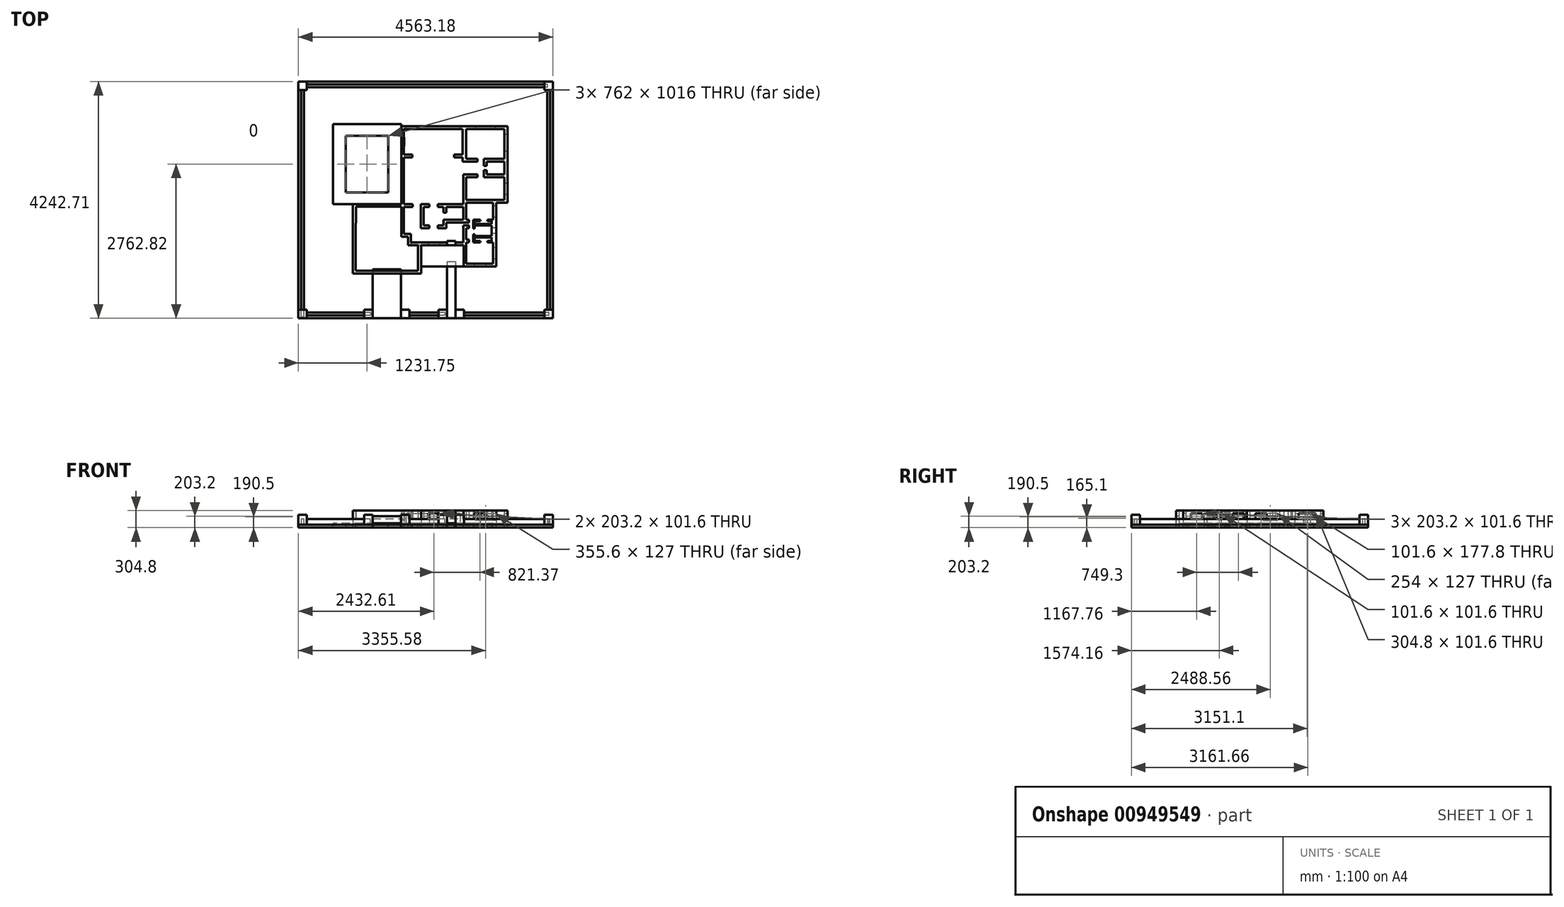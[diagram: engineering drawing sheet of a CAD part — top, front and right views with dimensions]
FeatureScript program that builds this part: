
annotation { "Feature Type Name" : "Feature", "Feature Type Description" : "" }
export const myFeature = defineFeature(function(context is Context, id is Id, definition is map)
    precondition{}
    {
        {
            var Q0;
            Q0=qCreatedBy(makeId("Top.planeOp"),FACE);
            var sketch = newSketch(context, id + "F0", { "sketchPlane" : qUnion([Q0])});
            skLineSegment(sketch, "E0", {"start": v(0, 0) * mm, "end": v(533.4, 0) * mm});
            skLineSegment(sketch, "E1", {"start": v(1396.8, 508) * mm, "end": v(1396.8, 127) * mm});
            skLineSegment(sketch, "E2", {"start": v(1396.8, 127) * mm, "end": v(1879.4, 127) * mm});
            skLineSegment(sketch, "E3", {"start": v(1828.6, 1270) * mm, "end": v(2082.6, 1270) * mm});
            skLineSegment(sketch, "E4", {"start": v(2082.6, 2540) * mm, "end": v(1396.8, 2540) * mm});
            skLineSegment(sketch, "E5", {"start": v(231.53, 1150.6) * mm, "end": v(-301.87, 1150.6) * mm});
            skLineSegment(sketch, "E6", {"start": v(-304.8, 1192.71) * mm, "end": v(177.8, 1192.71) * mm});
            skLineSegment(sketch, "E7", {"start": v(-47.87, -51.89) * mm, "end": v(587.13, -51.89) * mm});
            skLineSegment(sketch, "E8", {"start": v(587.13, -51.89) * mm, "end": v(587.13, 456.11) * mm});
            skLineSegment(sketch, "E9", {"start": v(587.13, 456.11) * mm, "end": v(1349.13, 456.11) * mm});
            skLineSegment(sketch, "E10", {"start": v(1349.13, 456.11) * mm, "end": v(1349.13, 75.11) * mm});
            skLineSegment(sketch, "E11", {"start": v(1349.13, 75.11) * mm, "end": v(1933.33, 75.11) * mm});
            skLineSegment(sketch, "E12", {"start": v(2136.53, 1218.11) * mm, "end": v(2136.53, 2589.71) * mm});
            skLineSegment(sketch, "E13", {"start": v(2136.53, 2589.71) * mm, "end": v(1349.13, 2589.71) * mm});
            skLineSegment(sketch, "E14", {"start": v(533.4, 456.11) * mm, "end": v(482.6, 456.11) * mm});
            skLineSegment(sketch, "E15", {"start": v(482.6, 456.11) * mm, "end": v(355.6, 456.11) * mm});
            skLineSegment(sketch, "E16", {"start": v(355.6, 456.11) * mm, "end": v(355.6, 608.51) * mm});
            skLineSegment(sketch, "E17", {"start": v(355.6, 608.51) * mm, "end": v(231.53, 608.51) * mm});
            skLineSegment(sketch, "E18", {"start": v(231.53, 608.51) * mm, "end": v(231.53, 1150.6) * mm});
            skLineSegment(sketch, "E19", {"start": v(279.4, 1143) * mm, "end": v(279.4, 660.4) * mm});
            skLineSegment(sketch, "E20", {"start": v(406.4, 508) * mm, "end": v(533.4, 508) * mm});
            skLineSegment(sketch, "E21", {"start": v(177.8, 1192.71) * mm, "end": v(231.53, 1192.71) * mm});
            skLineSegment(sketch, "E22", {"start": v(231.53, 1192.71) * mm, "end": v(231.53, 2081.71) * mm});
            skLineSegment(sketch, "E23", {"start": v(533.4, 456.11) * mm, "end": v(533.4, 0) * mm});
            skLineSegment(sketch, "E24", {"start": v(1828.6, 1219.2) * mm, "end": v(1396.8, 1219.2) * mm});
            skLineSegment(sketch, "E25", {"start": v(1933.33, 75.11) * mm, "end": v(1933.33, 1218.11) * mm});
            skLineSegment(sketch, "E26", {"start": v(1933.33, 1218.11) * mm, "end": v(2136.53, 1218.11) * mm});
            skLineSegment(sketch, "E27", {"start": v(1879.4, 127) * mm, "end": v(1879.4, 1219.2) * mm});
            skLineSegment(sketch, "E28", {"start": v(1879.4, 1219.2) * mm, "end": v(1828.6, 1219.2) * mm});
            skLineSegment(sketch, "E29", {"start": v(1396.8, 508) * mm, "end": v(1447.6, 508) * mm});
            skLineSegment(sketch, "E30", {"start": v(1523.8, 508) * mm, "end": v(1650.8, 508) * mm});
            skLineSegment(sketch, "E31", {"start": v(1879.4, 508) * mm, "end": v(1777.8, 508) * mm});
            skLineSegment(sketch, "E32", {"start": v(1523.8, 508) * mm, "end": v(1523.8, 596.9) * mm});
            skLineSegment(sketch, "E33", {"start": v(1879.4, 811.34) * mm, "end": v(1879.4, 749.31) * mm});
            skLineSegment(sketch, "E34", {"start": v(1523.8, 914.4) * mm, "end": v(1650.8, 914.4) * mm});
            skLineSegment(sketch, "E35", {"start": v(1879.4, 914.4) * mm, "end": v(1777.8, 914.4) * mm});
            skLineSegment(sketch, "E36", {"start": v(1523.8, 596.9) * mm, "end": v(1523.8, 650.75) * mm});
            skLineSegment(sketch, "E37", {"start": v(1523.8, 811.34) * mm, "end": v(1523.8, 757.49) * mm});
            skLineSegment(sketch, "E38", {"start": v(1396.8, 965.2) * mm, "end": v(1396.8, 1219.2) * mm});
            skLineSegment(sketch, "E39", {"start": v(1650.8, 914.4) * mm, "end": v(1650.8, 889) * mm});
            skLineSegment(sketch, "E40", {"start": v(1650.8, 889) * mm, "end": v(1549.2, 889) * mm});
            skLineSegment(sketch, "E41", {"start": v(1549.2, 889) * mm, "end": v(1549.2, 838.2) * mm});
            skLineSegment(sketch, "E42", {"start": v(1549.2, 838.2) * mm, "end": v(1854, 838.2) * mm});
            skLineSegment(sketch, "E43", {"start": v(1854, 838.2) * mm, "end": v(1854, 889) * mm});
            skLineSegment(sketch, "E44", {"start": v(1854, 889) * mm, "end": v(1777.8, 889) * mm});
            skLineSegment(sketch, "E45", {"start": v(1777.8, 889) * mm, "end": v(1777.8, 914.4) * mm});
            skLineSegment(sketch, "E46", {"start": v(1523.8, 757.49) * mm, "end": v(1549.2, 757.49) * mm});
            skLineSegment(sketch, "E47", {"start": v(1549.2, 757.49) * mm, "end": v(1549.2, 811.34) * mm});
            skLineSegment(sketch, "E48", {"start": v(1549.2, 811.34) * mm, "end": v(1854, 811.34) * mm});
            skLineSegment(sketch, "E49", {"start": v(1854, 811.34) * mm, "end": v(1854, 622.3) * mm});
            skLineSegment(sketch, "E50", {"start": v(1854, 622.3) * mm, "end": v(1549.2, 622.3) * mm});
            skLineSegment(sketch, "E51", {"start": v(1549.2, 622.3) * mm, "end": v(1549.2, 650.75) * mm});
            skLineSegment(sketch, "E52", {"start": v(1549.2, 650.75) * mm, "end": v(1523.8, 650.75) * mm});
            skLineSegment(sketch, "E53", {"start": v(1650.8, 508) * mm, "end": v(1650.8, 533.4) * mm});
            skLineSegment(sketch, "E54", {"start": v(1650.8, 533.4) * mm, "end": v(1549.2, 533.4) * mm});
            skLineSegment(sketch, "E55", {"start": v(1549.2, 533.4) * mm, "end": v(1549.2, 596.9) * mm});
            skLineSegment(sketch, "E56", {"start": v(1549.2, 596.9) * mm, "end": v(1854, 596.9) * mm});
            skLineSegment(sketch, "E57", {"start": v(1854, 596.9) * mm, "end": v(1854, 533.4) * mm});
            skLineSegment(sketch, "E58", {"start": v(1854, 533.4) * mm, "end": v(1777.8, 533.4) * mm});
            skLineSegment(sketch, "E59", {"start": v(1777.8, 533.4) * mm, "end": v(1777.8, 508) * mm});
            skLineSegment(sketch, "E60", {"start": v(1447.6, 508) * mm, "end": v(1447.6, 558.8) * mm});
            skLineSegment(sketch, "E61", {"start": v(1447.6, 558.8) * mm, "end": v(1396.8, 558.8) * mm});
            skLineSegment(sketch, "E62", {"start": v(1396.8, 558.8) * mm, "end": v(1396.8, 762) * mm});
            skLineSegment(sketch, "E63", {"start": v(1396.8, 965.2) * mm, "end": v(1396.8, 914.4) * mm});
            skLineSegment(sketch, "E64", {"start": v(1714.5, 1678.02) * mm, "end": v(2082.6, 1678.02) * mm});
            skLineSegment(sketch, "E65", {"start": v(1331.87, 2032) * mm, "end": v(1331.87, 1957.42) * mm});
            skLineSegment(sketch, "E66", {"start": v(1331.87, 1957.42) * mm, "end": v(1600.2, 1957.42) * mm});
            skLineSegment(sketch, "E67", {"start": v(1600.2, 1957.42) * mm, "end": v(1600.2, 2008.22) * mm});
            skLineSegment(sketch, "E68", {"start": v(1600.2, 2008.22) * mm, "end": v(1396.8, 2008.22) * mm});
            skLineSegment(sketch, "E69", {"start": v(1396.8, 2008.22) * mm, "end": v(1396.8, 2540) * mm});
            skLineSegment(sketch, "E70", {"start": v(1714.5, 1957.42) * mm, "end": v(1714.5, 2008.22) * mm});
            skLineSegment(sketch, "E71", {"start": v(1714.5, 2008.22) * mm, "end": v(2082.6, 2008.22) * mm});
            skLineSegment(sketch, "E72", {"start": v(2082.6, 2008.22) * mm, "end": v(2082.6, 2540) * mm});
            skLineSegment(sketch, "E73", {"start": v(1714.5, 1678.02) * mm, "end": v(1714.5, 1728.82) * mm});
            skLineSegment(sketch, "E74", {"start": v(2082.6, 1728.82) * mm, "end": v(2082.6, 1957.42) * mm});
            skLineSegment(sketch, "E75", {"start": v(2082.6, 1270) * mm, "end": v(2082.6, 1678.02) * mm});
            skLineSegment(sketch, "E76", {"start": v(1828.6, 1270) * mm, "end": v(1396.8, 1270) * mm});
            skLineSegment(sketch, "E77", {"start": v(1396.8, 1270) * mm, "end": v(1396.8, 1678.02) * mm});
            skLineSegment(sketch, "E78", {"start": v(1346, 1574.8) * mm, "end": v(1346, 1728.82) * mm});
            skLineSegment(sketch, "E79", {"start": v(1346, 1728.82) * mm, "end": v(1600.2, 1728.82) * mm});
            skLineSegment(sketch, "E80", {"start": v(1600.2, 1728.82) * mm, "end": v(1600.2, 1678.02) * mm});
            skLineSegment(sketch, "E81", {"start": v(1600.2, 1678.02) * mm, "end": v(1396.8, 1678.02) * mm});
            skLineSegment(sketch, "E82", {"start": v(1714.5, 1957.42) * mm, "end": v(1714.5, 1881.22) * mm});
            skLineSegment(sketch, "E83", {"start": v(1714.5, 1728.82) * mm, "end": v(1714.5, 1805.02) * mm});
            skLineSegment(sketch, "E84", {"start": v(1714.5, 1805.02) * mm, "end": v(1765.3, 1805.02) * mm});
            skLineSegment(sketch, "E85", {"start": v(1765.3, 1805.02) * mm, "end": v(1765.3, 1728.82) * mm});
            skLineSegment(sketch, "E86", {"start": v(1765.3, 1728.82) * mm, "end": v(2082.6, 1728.82) * mm});
            skLineSegment(sketch, "E87", {"start": v(1714.5, 1881.22) * mm, "end": v(1765.3, 1881.22) * mm});
            skLineSegment(sketch, "E88", {"start": v(1765.3, 1881.22) * mm, "end": v(1765.3, 1957.42) * mm});
            skLineSegment(sketch, "E89", {"start": v(1765.3, 1957.42) * mm, "end": v(2082.6, 1957.42) * mm});
            skLineSegment(sketch, "E90", {"start": v(-635, 508) * mm, "end": v(-635, 1192.71) * mm});
            skLineSegment(sketch, "E91", {"start": v(-635, 1192.71) * mm, "end": v(-304.8, 1192.71) * mm});
            skLineSegment(sketch, "E92", {"start": v(-301.87, 1150.6) * mm, "end": v(-581.27, 1150.6) * mm});
            skLineSegment(sketch, "E93", {"start": v(-584.2, 558.8) * mm, "end": v(-581.27, 1150.6) * mm});
            skLineSegment(sketch, "E94", {"start": v(-47.87, -51.89) * mm, "end": v(-635, -51.89) * mm});
            skLineSegment(sketch, "E95", {"start": v(-635, -51.89) * mm, "end": v(-635, 508) * mm});
            skLineSegment(sketch, "E96", {"start": v(0, 0) * mm, "end": v(-584.2, 0) * mm});
            skLineSegment(sketch, "E97", {"start": v(-584.2, 0) * mm, "end": v(-584.2, 558.8) * mm});
            skLineSegment(sketch, "E98", {"start": v(1331.87, 2032) * mm, "end": v(1179.47, 2032) * mm});
            skLineSegment(sketch, "E99", {"start": v(1179.47, 2032) * mm, "end": v(1179.47, 2081.71) * mm});
            skLineSegment(sketch, "E100", {"start": v(279.4, 2032) * mm, "end": v(431.8, 2032) * mm});
            skLineSegment(sketch, "E101", {"start": v(431.8, 2032) * mm, "end": v(431.8, 2081.71) * mm});
            skLineSegment(sketch, "E102", {"start": v(431.8, 2081.71) * mm, "end": v(279.4, 2081.71) * mm});
            skLineSegment(sketch, "E103", {"start": v(1179.47, 2081.71) * mm, "end": v(1331.87, 2081.71) * mm});
            skLineSegment(sketch, "E104", {"start": v(1331.87, 2081.71) * mm, "end": v(1331.87, 2540) * mm});
            skLineSegment(sketch, "E105", {"start": v(1331.87, 2540) * mm, "end": v(1179.47, 2540) * mm});
            skLineSegment(sketch, "E106", {"start": v(1179.47, 2589.71) * mm, "end": v(1349.13, 2589.71) * mm});
            skLineSegment(sketch, "E107", {"start": v(231.53, 2081.71) * mm, "end": v(231.53, 2589.71) * mm});
            skLineSegment(sketch, "E108", {"start": v(231.53, 2589.71) * mm, "end": v(431.8, 2589.71) * mm});
            skLineSegment(sketch, "E109", {"start": v(431.8, 2538.91) * mm, "end": v(279.4, 2538.91) * mm});
            skLineSegment(sketch, "E110", {"start": v(279.4, 2538.91) * mm, "end": v(279.4, 2081.71) * mm});
            skLineSegment(sketch, "E111", {"start": v(1346, 762) * mm, "end": v(1346, 508) * mm});
            skLineSegment(sketch, "E112", {"start": v(1346, 508) * mm, "end": v(533.4, 508) * mm});
            skLineSegment(sketch, "E113", {"start": v(1346, 863.6) * mm, "end": v(1396.8, 863.6) * mm});
            skLineSegment(sketch, "E114", {"start": v(1523.8, 811.34) * mm, "end": v(1523.8, 863.6) * mm});
            skLineSegment(sketch, "E115", {"start": v(1523.8, 863.6) * mm, "end": v(1523.8, 914.4) * mm});
            skLineSegment(sketch, "E116", {"start": v(1396.8, 914.4) * mm, "end": v(1447.6, 914.4) * mm});
            skLineSegment(sketch, "E117", {"start": v(1447.6, 914.4) * mm, "end": v(1447.6, 863.6) * mm});
            skLineSegment(sketch, "E118", {"start": v(1447.6, 863.6) * mm, "end": v(1396.8, 863.6) * mm});
            skLineSegment(sketch, "E119", {"start": v(406.4, 508) * mm, "end": v(406.4, 660.4) * mm});
            skLineSegment(sketch, "E120", {"start": v(406.4, 660.4) * mm, "end": v(279.4, 660.4) * mm});
            skLineSegment(sketch, "E121", {"start": v(1396.8, 812.8) * mm, "end": v(1447.6, 812.8) * mm});
            skLineSegment(sketch, "E122", {"start": v(1447.6, 812.8) * mm, "end": v(1447.6, 762) * mm});
            skLineSegment(sketch, "E123", {"start": v(1447.6, 762) * mm, "end": v(1396.8, 762) * mm});
            skLineSegment(sketch, "E124", {"start": v(431.8, 2538.91) * mm, "end": v(1179.47, 2540) * mm});
            skLineSegment(sketch, "E125", {"start": v(1179.47, 2589.71) * mm, "end": v(431.8, 2589.71) * mm});
            skLineSegment(sketch, "E126", {"start": v(1346, 812.8) * mm, "end": v(1396.8, 812.8) * mm});
            skLineSegment(sketch, "E127", {"start": v(1346, 508) * mm, "end": v(1041.2, 508) * mm});
            skLineSegment(sketch, "E128", {"start": v(887.59, 812.8) * mm, "end": v(887.59, 762) * mm});
            skLineSegment(sketch, "E129", {"start": v(887.59, 812.8) * mm, "end": v(938.39, 812.8) * mm});
            skLineSegment(sketch, "E130", {"start": v(1346, 1574.8) * mm, "end": v(1346, 1320.8) * mm});
            skLineSegment(sketch, "E131", {"start": v(887.59, 762) * mm, "end": v(1039.99, 762) * mm});
            skLineSegment(sketch, "E132", {"start": v(1039.99, 762) * mm, "end": v(1039.99, 812.8) * mm});
            skLineSegment(sketch, "E133", {"start": v(1346, 1320.8) * mm, "end": v(1346, 1270) * mm});
            skLineSegment(sketch, "E134", {"start": v(735.19, 762) * mm, "end": v(582.79, 762) * mm});
            skLineSegment(sketch, "E135", {"start": v(582.79, 762) * mm, "end": v(582.79, 812.8) * mm});
            skLineSegment(sketch, "E136", {"start": v(735.19, 812.8) * mm, "end": v(735.19, 762) * mm});
            skLineSegment(sketch, "E137", {"start": v(279.4, 1143) * mm, "end": v(437.73, 1143) * mm});
            skLineSegment(sketch, "E138", {"start": v(735.19, 1143) * mm, "end": v(735.19, 1193.8) * mm});
            skLineSegment(sketch, "E139", {"start": v(735.19, 1193.8) * mm, "end": v(582.79, 1193.8) * mm});
            skLineSegment(sketch, "E140", {"start": v(582.79, 1193.8) * mm, "end": v(582.79, 1143) * mm});
            skLineSegment(sketch, "E141", {"start": v(437.73, 1143) * mm, "end": v(437.73, 1193.8) * mm});
            skLineSegment(sketch, "E142", {"start": v(437.73, 1193.8) * mm, "end": v(279.4, 1193.8) * mm});
            skLineSegment(sketch, "E143", {"start": v(938.39, 812.8) * mm, "end": v(989.19, 812.8) * mm});
            skLineSegment(sketch, "E144", {"start": v(582.79, 812.8) * mm, "end": v(582.79, 1143) * mm});
            skLineSegment(sketch, "E145", {"start": v(633.59, 1143) * mm, "end": v(633.59, 812.8) * mm});
            skLineSegment(sketch, "E146", {"start": v(1039.99, 1193.8) * mm, "end": v(887.59, 1193.8) * mm});
            skLineSegment(sketch, "E147", {"start": v(887.59, 1193.8) * mm, "end": v(887.59, 1143) * mm});
            skLineSegment(sketch, "E148", {"start": v(887.59, 1143) * mm, "end": v(989.19, 1143) * mm});
            skLineSegment(sketch, "E149", {"start": v(633.59, 1143) * mm, "end": v(735.19, 1143) * mm});
            skLineSegment(sketch, "E150", {"start": v(633.59, 812.8) * mm, "end": v(735.19, 812.8) * mm});
            skLineSegment(sketch, "E151", {"start": v(279.4, 2032) * mm, "end": v(279.4, 1193.8) * mm});
            skLineSegment(sketch, "E152", {"start": v(1346, 1193.8) * mm, "end": v(1193.6, 1193.8) * mm});
            skPoint(sketch, "E152.startSnap0", {"position": v(963.79, 1193.8) * mm});
            skPoint(sketch, "E152.endSnap0", {"position": v(358.57, 1193.8) * mm});
            skLineSegment(sketch, "E153", {"start": v(1193.6, 1143) * mm, "end": v(1346, 1143) * mm});
            skLineSegment(sketch, "E154", {"start": v(1346, 1193.8) * mm, "end": v(1346, 1270) * mm});
            skLineSegment(sketch, "E155", {"start": v(1346, 762) * mm, "end": v(1346, 812.8) * mm});
            skLineSegment(sketch, "E156", {"start": v(1039.99, 1193.8) * mm, "end": v(1193.6, 1193.8) * mm});
            skLineSegment(sketch, "E157", {"start": v(1193.6, 1143) * mm, "end": v(1039.99, 1143) * mm});
            skLineSegment(sketch, "E158", {"start": v(1039.99, 863.6) * mm, "end": v(1039.99, 812.8) * mm});
            skLineSegment(sketch, "E159", {"start": v(1346, 939.8) * mm, "end": v(1346, 1117.6) * mm});
            skLineSegment(sketch, "E160", {"start": v(1346, 1117.6) * mm, "end": v(1346, 1143) * mm});
            skLineSegment(sketch, "E161", {"start": v(1346, 914.4) * mm, "end": v(1346, 939.8) * mm});
            skLineSegment(sketch, "E162", {"start": v(1346, 863.6) * mm, "end": v(1039.99, 863.6) * mm});
            skLineSegment(sketch, "E163", {"start": v(1346, 914.4) * mm, "end": v(1039.99, 914.4) * mm});
            skLineSegment(sketch, "E164", {"start": v(989.19, 914.4) * mm, "end": v(1039.99, 914.4) * mm});
            skLineSegment(sketch, "E165", {"start": v(989.19, 812.8) * mm, "end": v(989.19, 914.4) * mm});
            skLineSegment(sketch, "E166", {"start": v(989.19, 1143) * mm, "end": v(989.19, 1041.4) * mm});
            skLineSegment(sketch, "E167", {"start": v(989.19, 1041.4) * mm, "end": v(1039.99, 1041.4) * mm});
            skLineSegment(sketch, "E168", {"start": v(1039.99, 1041.4) * mm, "end": v(1039.99, 1143) * mm});
            skSolve(sketch);
        }
        {
            var Q0;
            Q0=makeQuery(id+"F0.imprint","IMPRINT",FACE,{"disambiguationData":[TD([[makeQuery(id+"F0.imprint","IMPRINT",EDGE,{"derivedFrom":sQuery(id+"F0.wireOp",EDGE,"E0")}),-1.0]])]});
            var Q1;
            Q1=makeQuery(id+"F0.imprint","IMPRINT",FACE,{"disambiguationData":[TD([[makeQuery(id+"F0.imprint","IMPRINT",EDGE,{"derivedFrom":sQuery(id+"F0.wireOp",EDGE,"E30")}),1.0]])]});
            extrude(context, id + "F1", {"entities" : qUnion([Q0, Q1]), "depth" : 254 * mm, "offsetDistance" : 25.4 * mm});
        }
        {
            var Q0;
            Q0=qSketchRegion(id+"F0",true);
            var Q1;
            Q1=makeQuery(id+"F0.imprint","IMPRINT",FACE,{"disambiguationData":[TD([[makeQuery(id+"F0.imprint","IMPRINT",EDGE,{"derivedFrom":sQuery(id+"F0.wireOp",EDGE,"E134")}),-1.0]])]});
            var Q2;
            Q2=makeQuery(id+"F0.imprint","IMPRINT",FACE,{"disambiguationData":[TD([[makeQuery(id+"F0.imprint","IMPRINT",EDGE,{"derivedFrom":sQuery(id+"F0.wireOp",EDGE,"E128")}),1.0]])]});
            extrude(context, id + "F2", {"entities" : qUnion([Q0, Q1, Q2]), "operationType" : NewBodyOperationType.ADD, "depth" : 254 * mm, "offsetDistance" : 25.4 * mm});
        }
        {
            var Q0;
            Q0=makeQuery(id+"F1.opExtrude","CAP_FACE",FACE,{"disambiguationData":[OSD([sQuery(id+"F0.wireOp",EDGE,"E0"),sQuery(id+"F0.wireOp",EDGE,"E1"),sQuery(id+"F0.wireOp",EDGE,"E2"),sQuery(id+"F0.wireOp",EDGE,"E3"),sQuery(id+"F0.wireOp",EDGE,"E4"),sQuery(id+"F0.wireOp",EDGE,"E5"),sQuery(id+"F0.wireOp",EDGE,"E6"),sQuery(id+"F0.wireOp",EDGE,"E7"),sQuery(id+"F0.wireOp",EDGE,"E8"),sQuery(id+"F0.wireOp",EDGE,"E9"),sQuery(id+"F0.wireOp",EDGE,"E10"),sQuery(id+"F0.wireOp",EDGE,"E11"),sQuery(id+"F0.wireOp",EDGE,"E12"),sQuery(id+"F0.wireOp",EDGE,"E13"),sQuery(id+"F0.wireOp",EDGE,"E14"),sQuery(id+"F0.wireOp",EDGE,"E15"),sQuery(id+"F0.wireOp",EDGE,"E16"),sQuery(id+"F0.wireOp",EDGE,"E17"),sQuery(id+"F0.wireOp",EDGE,"E18"),sQuery(id+"F0.wireOp",EDGE,"E19"),sQuery(id+"F0.wireOp",EDGE,"E20"),sQuery(id+"F0.wireOp",EDGE,"E21"),sQuery(id+"F0.wireOp",EDGE,"E22"),sQuery(id+"F0.wireOp",EDGE,"E23"),sQuery(id+"F0.wireOp",EDGE,"E24"),sQuery(id+"F0.wireOp",EDGE,"E25"),sQuery(id+"F0.wireOp",EDGE,"E26"),sQuery(id+"F0.wireOp",EDGE,"E27"),sQuery(id+"F0.wireOp",EDGE,"E28"),sQuery(id+"F0.wireOp",EDGE,"E29"),sQuery(id+"F0.wireOp",EDGE,"E30"),sQuery(id+"F0.wireOp",EDGE,"E31"),sQuery(id+"F0.wireOp",EDGE,"E32"),sQuery(id+"F0.wireOp",EDGE,"E34"),sQuery(id+"F0.wireOp",EDGE,"E35"),sQuery(id+"F0.wireOp",EDGE,"E36"),sQuery(id+"F0.wireOp",EDGE,"E37"),sQuery(id+"F0.wireOp",EDGE,"E38"),sQuery(id+"F0.wireOp",EDGE,"E39"),sQuery(id+"F0.wireOp",EDGE,"E40"),sQuery(id+"F0.wireOp",EDGE,"E41"),sQuery(id+"F0.wireOp",EDGE,"E42"),sQuery(id+"F0.wireOp",EDGE,"E43"),sQuery(id+"F0.wireOp",EDGE,"E44"),sQuery(id+"F0.wireOp",EDGE,"E45"),sQuery(id+"F0.wireOp",EDGE,"E46"),sQuery(id+"F0.wireOp",EDGE,"E47"),sQuery(id+"F0.wireOp",EDGE,"E48"),sQuery(id+"F0.wireOp",EDGE,"E49"),sQuery(id+"F0.wireOp",EDGE,"E50"),sQuery(id+"F0.wireOp",EDGE,"E51"),sQuery(id+"F0.wireOp",EDGE,"E52"),sQuery(id+"F0.wireOp",EDGE,"E53"),sQuery(id+"F0.wireOp",EDGE,"E54"),sQuery(id+"F0.wireOp",EDGE,"E55"),sQuery(id+"F0.wireOp",EDGE,"E56"),sQuery(id+"F0.wireOp",EDGE,"E57"),sQuery(id+"F0.wireOp",EDGE,"E58"),sQuery(id+"F0.wireOp",EDGE,"E59"),sQuery(id+"F0.wireOp",EDGE,"E60"),sQuery(id+"F0.wireOp",EDGE,"E61"),sQuery(id+"F0.wireOp",EDGE,"E62"),sQuery(id+"F0.wireOp",EDGE,"E63"),sQuery(id+"F0.wireOp",EDGE,"E64"),sQuery(id+"F0.wireOp",EDGE,"E65"),sQuery(id+"F0.wireOp",EDGE,"E66"),sQuery(id+"F0.wireOp",EDGE,"E67"),sQuery(id+"F0.wireOp",EDGE,"E68"),sQuery(id+"F0.wireOp",EDGE,"E69"),sQuery(id+"F0.wireOp",EDGE,"E70"),sQuery(id+"F0.wireOp",EDGE,"E71"),sQuery(id+"F0.wireOp",EDGE,"E72"),sQuery(id+"F0.wireOp",EDGE,"E73"),sQuery(id+"F0.wireOp",EDGE,"E74"),sQuery(id+"F0.wireOp",EDGE,"E75"),sQuery(id+"F0.wireOp",EDGE,"E76"),sQuery(id+"F0.wireOp",EDGE,"E77"),sQuery(id+"F0.wireOp",EDGE,"E78"),sQuery(id+"F0.wireOp",EDGE,"E79"),sQuery(id+"F0.wireOp",EDGE,"E80"),sQuery(id+"F0.wireOp",EDGE,"E81"),sQuery(id+"F0.wireOp",EDGE,"E82"),sQuery(id+"F0.wireOp",EDGE,"E83"),sQuery(id+"F0.wireOp",EDGE,"E84"),sQuery(id+"F0.wireOp",EDGE,"E85"),sQuery(id+"F0.wireOp",EDGE,"E86"),sQuery(id+"F0.wireOp",EDGE,"E87"),sQuery(id+"F0.wireOp",EDGE,"E88"),sQuery(id+"F0.wireOp",EDGE,"E89"),sQuery(id+"F0.wireOp",EDGE,"E90"),sQuery(id+"F0.wireOp",EDGE,"E91"),sQuery(id+"F0.wireOp",EDGE,"E92"),sQuery(id+"F0.wireOp",EDGE,"E93"),sQuery(id+"F0.wireOp",EDGE,"E94"),sQuery(id+"F0.wireOp",EDGE,"E95"),sQuery(id+"F0.wireOp",EDGE,"E96"),sQuery(id+"F0.wireOp",EDGE,"E97"),sQuery(id+"F0.wireOp",EDGE,"E98"),sQuery(id+"F0.wireOp",EDGE,"E99"),sQuery(id+"F0.wireOp",EDGE,"E100"),sQuery(id+"F0.wireOp",EDGE,"E101"),sQuery(id+"F0.wireOp",EDGE,"E102"),sQuery(id+"F0.wireOp",EDGE,"E103"),sQuery(id+"F0.wireOp",EDGE,"E104"),sQuery(id+"F0.wireOp",EDGE,"E105"),sQuery(id+"F0.wireOp",EDGE,"E106"),sQuery(id+"F0.wireOp",EDGE,"E107"),sQuery(id+"F0.wireOp",EDGE,"E108"),sQuery(id+"F0.wireOp",EDGE,"E109"),sQuery(id+"F0.wireOp",EDGE,"E110"),sQuery(id+"F0.wireOp",EDGE,"E111"),sQuery(id+"F0.wireOp",EDGE,"E112"),sQuery(id+"F0.wireOp",EDGE,"E113"),sQuery(id+"F0.wireOp",EDGE,"E114"),sQuery(id+"F0.wireOp",EDGE,"E115"),sQuery(id+"F0.wireOp",EDGE,"E116"),sQuery(id+"F0.wireOp",EDGE,"E117"),sQuery(id+"F0.wireOp",EDGE,"E118"),sQuery(id+"F0.wireOp",EDGE,"E119"),sQuery(id+"F0.wireOp",EDGE,"E120"),sQuery(id+"F0.wireOp",EDGE,"E121"),sQuery(id+"F0.wireOp",EDGE,"E122"),sQuery(id+"F0.wireOp",EDGE,"E123"),sQuery(id+"F0.wireOp",EDGE,"E124"),sQuery(id+"F0.wireOp",EDGE,"E125"),sQuery(id+"F0.wireOp",EDGE,"E126"),sQuery(id+"F0.wireOp",EDGE,"E127"),sQuery(id+"F0.wireOp",EDGE,"E130"),sQuery(id+"F0.wireOp",EDGE,"wEKJqsZE-Lnf2-Pc3B-vstB-3JEagEBnImep"),sQuery(id+"F0.wireOp",EDGE,"E133"),sQuery(id+"F0.wireOp",EDGE,"E137"),sQuery(id+"F0.wireOp",EDGE,"E141"),sQuery(id+"F0.wireOp",EDGE,"E142"),sQuery(id+"F0.wireOp",EDGE,"E151"),sQuery(id+"F0.wireOp",EDGE,"E152"),sQuery(id+"F0.wireOp",EDGE,"XqZMZlJO-xrwS-6yc9-YKlE-u4GM9skw6DG2"),sQuery(id+"F0.wireOp",EDGE,"E153"),sQuery(id+"F0.wireOp",EDGE,"E154"),sQuery(id+"F0.wireOp",EDGE,"MRLSVep9-wh13-aC8x-J69K-2GoYUCsBfXyJ"),sQuery(id+"F0.wireOp",EDGE,"E155")])],"isStart":true});
            var sketch = newSketch(context, id + "F3", { "sketchPlane" : qUnion([Q0])});
            skSolve(sketch);
        }
        {
            var Q0;
            Q0=makeQuery(id+"F3.imprint","IMPRINT",FACE,{"disambiguationData":[TD([[makeQuery(id+"F3.imprint","IMPRINT",EDGE,{"derivedFrom":makeQuery(id+"F1.opExtrude","CAP_EDGE",EDGE,{"disambiguationData":[OSD([sQuery(id+"F0.wireOp",EDGE,"E16")])],"isStart":true})}),-1.0]])]});
            var Q1;
            Q1=makeQuery(id+"F3.imprint","IMPRINT",FACE,{"disambiguationData":[TD([[makeQuery(id+"F3.imprint","IMPRINT",EDGE,{"derivedFrom":makeQuery(id+"F1.opExtrude","CAP_EDGE",EDGE,{"disambiguationData":[OSD([sQuery(id+"F0.wireOp",EDGE,"E1")])],"isStart":true})}),-1.0]])]});
            extrude(context, id + "F4", {"entities" : qUnion([Q0, Q1]), "oppositeDirection" : true, "depth" : 25.4 * mm, "offsetDistance" : 25.4 * mm});
        }
        {
            var Q0;
            Q0=makeQuery(id+"F1.opExtrude","SWEPT_FACE",FACE,{"disambiguationData":[OSD([sQuery(id+"F0.wireOp",EDGE,"E18")])]});
            var sketch = newSketch(context, id + "F5", { "sketchPlane" : qUnion([Q0])});
            skLineSegment(sketch, "E169", {"start": v(-608.51, 254) * mm, "end": v(-879.56, 254) * mm});
            skLineSegment(sketch, "E170", {"start": v(-879.56, 254) * mm, "end": v(-981.16, 254) * mm});
            skLineSegment(sketch, "E171", {"start": v(-981.16, 254) * mm, "end": v(-777.96, 254) * mm});
            skLineSegment(sketch, "E172", {"start": v(-777.96, 254) * mm, "end": v(-777.96, 25.4) * mm});
            skLineSegment(sketch, "E173", {"start": v(-777.96, 25.4) * mm, "end": v(-981.16, 25.4) * mm});
            skLineSegment(sketch, "E174", {"start": v(-981.16, 25.4) * mm, "end": v(-981.16, 254) * mm});
            skLineSegment(sketch, "E175", {"start": v(-981.16, 254) * mm, "end": v(-981.16, 203.2) * mm});
            skLineSegment(sketch, "E176", {"start": v(-981.16, 203.2) * mm, "end": v(-777.96, 203.2) * mm});
            skLineSegment(sketch, "E177", {"start": v(-777.96, 203.2) * mm, "end": v(-777.96, 254) * mm});
            skSolve(sketch);
        }
        {
            var Q0;
            Q0=qSketchRegion(id+"F5",true);
            extrude(context, id + "F6", {"entities" : qUnion([Q0]), "operationType" : NewBodyOperationType.REMOVE, "oppositeDirection" : true, "depth" : 50.8 * mm, "offsetDistance" : 25.4 * mm});
        }
        {
            var Q0;
            Q0=makeQuery(id+"F1.opExtrude","SWEPT_FACE",FACE,{"disambiguationData":[OSD([sQuery(id+"F0.wireOp",EDGE,"E9")])]});
            var sketch = newSketch(context, id + "F7", { "sketchPlane" : qUnion([Q0])});
            skLineSegment(sketch, "E178", {"start": v(1052.6, 0) * mm, "end": v(1052.6, 254) * mm});
            skLineSegment(sketch, "E179", {"start": v(1052.6, 254) * mm, "end": v(1205, 254) * mm});
            skLineSegment(sketch, "E180", {"start": v(1205, 254) * mm, "end": v(1205, 0) * mm});
            skLineSegment(sketch, "E181", {"start": v(1205, 0) * mm, "end": v(1052.6, 0) * mm});
            skSolve(sketch);
        }
        {
            var Q0;
            Q0=qSketchRegion(id+"F7",true);
            extrude(context, id + "F8", {"entities" : qUnion([Q0]), "operationType" : NewBodyOperationType.REMOVE, "oppositeDirection" : true, "depth" : 76.2 * mm, "offsetDistance" : 25.4 * mm});
        }
        {
            var Q0;
            Q0=makeQuery(id+"F4.opExtrude","SWEPT_FACE",FACE,{"disambiguationData":[OSD([sQuery(id+"F0.wireOp",EDGE,"E20"),sQuery(id+"F0.wireOp",EDGE,"E112"),sQuery(id+"F0.wireOp",EDGE,"E127")])]});
            var sketch = newSketch(context, id + "F9", { "sketchPlane" : qUnion([Q0])});
            skSolve(sketch);
        }
        {
            var Q0;
            Q0=qSketchRegion(id+"F9",true);
            var Q1;
            {var subQ0=sQuery(id+"F0.wireOp",EDGE,"E127");var subQ1=sQuery(id+"F0.wireOp",EDGE,"E112");var subQ2=sQuery(id+"F0.wireOp",EDGE,"E20");Q1=makeQuery(id+"F9.imprint","IMPRINT",FACE,{"disambiguationData":[TD([[makeQuery(id+"F9.imprint","IMPRINT",EDGE,{"derivedFrom":makeQuery(id+"F4.opExtrude","CAP_EDGE",EDGE,{"disambiguationData":[OSD([subQ2,subQ1,subQ0])],"isStart":true})}),-1.0]])]});}
            extrude(context, id + "F10", {"entities" : qUnion([Q0, Q1]), "depth" : 53.34 * mm, "offsetDistance" : 25.4 * mm});
        }
        {
            var Q0;
            {var subQ130=sQuery(id+"F0.wireOp",EDGE,"E9");var subQ131=sQuery(id+"F0.wireOp",EDGE,"E8");Q0=makeQuery(id+"F8.boolean.opBoolean","SPLIT",FACE,{"disambiguationData":[TD([makeQuery(id+"F1.opExtrude","SWEPT_FACE",FACE,{"disambiguationData":[OSD([subQ131])]})])],"derivedFrom":makeQuery(id+"F1.opExtrude","SWEPT_FACE",FACE,{"disambiguationData":[OSD([subQ130])]})});}
            var sketch = newSketch(context, id + "F11", { "sketchPlane" : qUnion([Q0])});
            skLineSegment(sketch, "E182", {"start": v(819.86, 203.2) * mm, "end": v(718.26, 203.2) * mm});
            skLineSegment(sketch, "E183", {"start": v(718.26, 203.2) * mm, "end": v(718.26, 101.6) * mm});
            skLineSegment(sketch, "E184", {"start": v(718.26, 101.6) * mm, "end": v(921.46, 101.6) * mm});
            skLineSegment(sketch, "E185", {"start": v(921.46, 101.6) * mm, "end": v(921.46, 203.2) * mm});
            skLineSegment(sketch, "E186", {"start": v(921.46, 203.2) * mm, "end": v(819.86, 203.2) * mm});
            skSolve(sketch);
        }
        {
            var Q0;
            Q0=qSketchRegion(id+"F11",true);
            extrude(context, id + "F12", {"entities" : qUnion([Q0]), "operationType" : NewBodyOperationType.REMOVE, "oppositeDirection" : true, "depth" : 63.5 * mm, "offsetDistance" : 25.4 * mm});
        }
        {
            var Q0;
            Q0=makeQuery(id+"F1.opExtrude","SWEPT_FACE",FACE,{"disambiguationData":[OSD([sQuery(id+"F0.wireOp",EDGE,"E11")])]});
            var sketch = newSketch(context, id + "F13", { "sketchPlane" : qUnion([Q0])});
            skLineSegment(sketch, "E187", {"start": v(1641.23, 203.2) * mm, "end": v(1539.63, 203.2) * mm});
            skLineSegment(sketch, "E188", {"start": v(1539.63, 203.2) * mm, "end": v(1539.63, 101.6) * mm});
            skLineSegment(sketch, "E189", {"start": v(1539.63, 101.6) * mm, "end": v(1742.83, 101.6) * mm});
            skLineSegment(sketch, "E190", {"start": v(1742.83, 101.6) * mm, "end": v(1742.83, 203.2) * mm});
            skLineSegment(sketch, "E191", {"start": v(1742.83, 203.2) * mm, "end": v(1641.23, 203.2) * mm});
            skSolve(sketch);
        }
        {
            var Q0;
            Q0=qSketchRegion(id+"F13",true);
            extrude(context, id + "F14", {"entities" : qUnion([Q0]), "operationType" : NewBodyOperationType.REMOVE, "oppositeDirection" : true, "depth" : 76.2 * mm, "offsetDistance" : 25.4 * mm});
        }
        {
            var Q0;
            Q0=makeQuery(id+"F1.opExtrude","SWEPT_FACE",FACE,{"disambiguationData":[OSD([sQuery(id+"F0.wireOp",EDGE,"E25")])]});
            var sketch = newSketch(context, id + "F15", { "sketchPlane" : qUnion([Q0])});
            skLineSegment(sketch, "E192", {"start": v(75.11, 254) * mm, "end": v(557.71, 254) * mm});
            skLineSegment(sketch, "E193", {"start": v(557.71, 254) * mm, "end": v(316.41, 254) * mm});
            skLineSegment(sketch, "E194", {"start": v(316.41, 203.2) * mm, "end": v(214.81, 203.2) * mm});
            skLineSegment(sketch, "E195", {"start": v(214.81, 203.2) * mm, "end": v(214.81, 101.6) * mm});
            skLineSegment(sketch, "E196", {"start": v(214.81, 101.6) * mm, "end": v(418.01, 101.6) * mm});
            skLineSegment(sketch, "E197", {"start": v(418.01, 101.6) * mm, "end": v(418.01, 203.2) * mm});
            skLineSegment(sketch, "E198", {"start": v(418.01, 203.2) * mm, "end": v(316.41, 203.2) * mm});
            skLineSegment(sketch, "E199", {"start": v(1218.11, 254) * mm, "end": v(913.31, 254) * mm});
            skLineSegment(sketch, "E200", {"start": v(1065.71, 203.2) * mm, "end": v(964.11, 203.2) * mm});
            skLineSegment(sketch, "E201", {"start": v(964.11, 203.2) * mm, "end": v(964.11, 101.6) * mm});
            skLineSegment(sketch, "E202", {"start": v(964.11, 101.6) * mm, "end": v(1167.31, 101.6) * mm});
            skLineSegment(sketch, "E203", {"start": v(1167.31, 101.6) * mm, "end": v(1167.31, 203.2) * mm});
            skLineSegment(sketch, "E204", {"start": v(1167.31, 203.2) * mm, "end": v(1065.71, 203.2) * mm});
            skLineSegment(sketch, "E205", {"start": v(913.31, 254) * mm, "end": v(862.51, 254) * mm});
            skLineSegment(sketch, "E206", {"start": v(862.51, 254) * mm, "end": v(557.71, 254) * mm});
            skLineSegment(sketch, "E207", {"start": v(710.11, 254) * mm, "end": v(710.11, 203.2) * mm});
            skLineSegment(sketch, "E208", {"start": v(710.11, 203.2) * mm, "end": v(672.01, 203.2) * mm});
            skLineSegment(sketch, "E209", {"start": v(672.01, 203.2) * mm, "end": v(672.01, 101.6) * mm});
            skLineSegment(sketch, "E210", {"start": v(672.01, 101.6) * mm, "end": v(773.61, 101.6) * mm});
            skLineSegment(sketch, "E211", {"start": v(773.61, 101.6) * mm, "end": v(773.61, 203.2) * mm});
            skLineSegment(sketch, "E212", {"start": v(773.61, 203.2) * mm, "end": v(710.11, 203.2) * mm});
            skSolve(sketch);
        }
        {
            var Q0;
            Q0=qSketchRegion(id+"F15",true);
            extrude(context, id + "F16", {"entities" : qUnion([Q0]), "operationType" : NewBodyOperationType.REMOVE, "oppositeDirection" : true, "depth" : 101.6 * mm, "offsetDistance" : 25.4 * mm});
        }
        {
            var Q0;
            Q0=makeQuery(id+"F1.opExtrude","CAP_FACE",FACE,{"disambiguationData":[OSD([sQuery(id+"F0.wireOp",EDGE,"E0"),sQuery(id+"F0.wireOp",EDGE,"E1"),sQuery(id+"F0.wireOp",EDGE,"E2"),sQuery(id+"F0.wireOp",EDGE,"E3"),sQuery(id+"F0.wireOp",EDGE,"E4"),sQuery(id+"F0.wireOp",EDGE,"E5"),sQuery(id+"F0.wireOp",EDGE,"E6"),sQuery(id+"F0.wireOp",EDGE,"E7"),sQuery(id+"F0.wireOp",EDGE,"E8"),sQuery(id+"F0.wireOp",EDGE,"E9"),sQuery(id+"F0.wireOp",EDGE,"E10"),sQuery(id+"F0.wireOp",EDGE,"E11"),sQuery(id+"F0.wireOp",EDGE,"E12"),sQuery(id+"F0.wireOp",EDGE,"E13"),sQuery(id+"F0.wireOp",EDGE,"E14"),sQuery(id+"F0.wireOp",EDGE,"E15"),sQuery(id+"F0.wireOp",EDGE,"E16"),sQuery(id+"F0.wireOp",EDGE,"E17"),sQuery(id+"F0.wireOp",EDGE,"E18"),sQuery(id+"F0.wireOp",EDGE,"E19"),sQuery(id+"F0.wireOp",EDGE,"E20"),sQuery(id+"F0.wireOp",EDGE,"E21"),sQuery(id+"F0.wireOp",EDGE,"E22"),sQuery(id+"F0.wireOp",EDGE,"E23"),sQuery(id+"F0.wireOp",EDGE,"E24"),sQuery(id+"F0.wireOp",EDGE,"E25"),sQuery(id+"F0.wireOp",EDGE,"E26"),sQuery(id+"F0.wireOp",EDGE,"E27"),sQuery(id+"F0.wireOp",EDGE,"E28"),sQuery(id+"F0.wireOp",EDGE,"E29"),sQuery(id+"F0.wireOp",EDGE,"E30"),sQuery(id+"F0.wireOp",EDGE,"E31"),sQuery(id+"F0.wireOp",EDGE,"E32"),sQuery(id+"F0.wireOp",EDGE,"E34"),sQuery(id+"F0.wireOp",EDGE,"E35"),sQuery(id+"F0.wireOp",EDGE,"E36"),sQuery(id+"F0.wireOp",EDGE,"E37"),sQuery(id+"F0.wireOp",EDGE,"E38"),sQuery(id+"F0.wireOp",EDGE,"E39"),sQuery(id+"F0.wireOp",EDGE,"E40"),sQuery(id+"F0.wireOp",EDGE,"E41"),sQuery(id+"F0.wireOp",EDGE,"E42"),sQuery(id+"F0.wireOp",EDGE,"E43"),sQuery(id+"F0.wireOp",EDGE,"E44"),sQuery(id+"F0.wireOp",EDGE,"E45"),sQuery(id+"F0.wireOp",EDGE,"E46"),sQuery(id+"F0.wireOp",EDGE,"E47"),sQuery(id+"F0.wireOp",EDGE,"E48"),sQuery(id+"F0.wireOp",EDGE,"E49"),sQuery(id+"F0.wireOp",EDGE,"E50"),sQuery(id+"F0.wireOp",EDGE,"E51"),sQuery(id+"F0.wireOp",EDGE,"E52"),sQuery(id+"F0.wireOp",EDGE,"E53"),sQuery(id+"F0.wireOp",EDGE,"E54"),sQuery(id+"F0.wireOp",EDGE,"E55"),sQuery(id+"F0.wireOp",EDGE,"E56"),sQuery(id+"F0.wireOp",EDGE,"E57"),sQuery(id+"F0.wireOp",EDGE,"E58"),sQuery(id+"F0.wireOp",EDGE,"E59"),sQuery(id+"F0.wireOp",EDGE,"E60"),sQuery(id+"F0.wireOp",EDGE,"E61"),sQuery(id+"F0.wireOp",EDGE,"E62"),sQuery(id+"F0.wireOp",EDGE,"E63"),sQuery(id+"F0.wireOp",EDGE,"E64"),sQuery(id+"F0.wireOp",EDGE,"E65"),sQuery(id+"F0.wireOp",EDGE,"E66"),sQuery(id+"F0.wireOp",EDGE,"E67"),sQuery(id+"F0.wireOp",EDGE,"E68"),sQuery(id+"F0.wireOp",EDGE,"E69"),sQuery(id+"F0.wireOp",EDGE,"E70"),sQuery(id+"F0.wireOp",EDGE,"E71"),sQuery(id+"F0.wireOp",EDGE,"E72"),sQuery(id+"F0.wireOp",EDGE,"E73"),sQuery(id+"F0.wireOp",EDGE,"E74"),sQuery(id+"F0.wireOp",EDGE,"E75"),sQuery(id+"F0.wireOp",EDGE,"E76"),sQuery(id+"F0.wireOp",EDGE,"E77"),sQuery(id+"F0.wireOp",EDGE,"E78"),sQuery(id+"F0.wireOp",EDGE,"E79"),sQuery(id+"F0.wireOp",EDGE,"E80"),sQuery(id+"F0.wireOp",EDGE,"E81"),sQuery(id+"F0.wireOp",EDGE,"E82"),sQuery(id+"F0.wireOp",EDGE,"E83"),sQuery(id+"F0.wireOp",EDGE,"E84"),sQuery(id+"F0.wireOp",EDGE,"E85"),sQuery(id+"F0.wireOp",EDGE,"E86"),sQuery(id+"F0.wireOp",EDGE,"E87"),sQuery(id+"F0.wireOp",EDGE,"E88"),sQuery(id+"F0.wireOp",EDGE,"E89"),sQuery(id+"F0.wireOp",EDGE,"E90"),sQuery(id+"F0.wireOp",EDGE,"E91"),sQuery(id+"F0.wireOp",EDGE,"E92"),sQuery(id+"F0.wireOp",EDGE,"E93"),sQuery(id+"F0.wireOp",EDGE,"E94"),sQuery(id+"F0.wireOp",EDGE,"E95"),sQuery(id+"F0.wireOp",EDGE,"E96"),sQuery(id+"F0.wireOp",EDGE,"E97"),sQuery(id+"F0.wireOp",EDGE,"E98"),sQuery(id+"F0.wireOp",EDGE,"E99"),sQuery(id+"F0.wireOp",EDGE,"E100"),sQuery(id+"F0.wireOp",EDGE,"E101"),sQuery(id+"F0.wireOp",EDGE,"E102"),sQuery(id+"F0.wireOp",EDGE,"E103"),sQuery(id+"F0.wireOp",EDGE,"E104"),sQuery(id+"F0.wireOp",EDGE,"E105"),sQuery(id+"F0.wireOp",EDGE,"E106"),sQuery(id+"F0.wireOp",EDGE,"E107"),sQuery(id+"F0.wireOp",EDGE,"E108"),sQuery(id+"F0.wireOp",EDGE,"E109"),sQuery(id+"F0.wireOp",EDGE,"E110"),sQuery(id+"F0.wireOp",EDGE,"E111"),sQuery(id+"F0.wireOp",EDGE,"E112"),sQuery(id+"F0.wireOp",EDGE,"E113"),sQuery(id+"F0.wireOp",EDGE,"E114"),sQuery(id+"F0.wireOp",EDGE,"E115"),sQuery(id+"F0.wireOp",EDGE,"E116"),sQuery(id+"F0.wireOp",EDGE,"E117"),sQuery(id+"F0.wireOp",EDGE,"E118"),sQuery(id+"F0.wireOp",EDGE,"E119"),sQuery(id+"F0.wireOp",EDGE,"E120"),sQuery(id+"F0.wireOp",EDGE,"E121"),sQuery(id+"F0.wireOp",EDGE,"E122"),sQuery(id+"F0.wireOp",EDGE,"E123"),sQuery(id+"F0.wireOp",EDGE,"E124"),sQuery(id+"F0.wireOp",EDGE,"E125"),sQuery(id+"F0.wireOp",EDGE,"E126"),sQuery(id+"F0.wireOp",EDGE,"E127"),sQuery(id+"F0.wireOp",EDGE,"E130"),sQuery(id+"F0.wireOp",EDGE,"wEKJqsZE-Lnf2-Pc3B-vstB-3JEagEBnImep"),sQuery(id+"F0.wireOp",EDGE,"E133"),sQuery(id+"F0.wireOp",EDGE,"E137"),sQuery(id+"F0.wireOp",EDGE,"E141"),sQuery(id+"F0.wireOp",EDGE,"E142"),sQuery(id+"F0.wireOp",EDGE,"E151"),sQuery(id+"F0.wireOp",EDGE,"E152"),sQuery(id+"F0.wireOp",EDGE,"XqZMZlJO-xrwS-6yc9-YKlE-u4GM9skw6DG2"),sQuery(id+"F0.wireOp",EDGE,"E153"),sQuery(id+"F0.wireOp",EDGE,"E154"),sQuery(id+"F0.wireOp",EDGE,"MRLSVep9-wh13-aC8x-J69K-2GoYUCsBfXyJ"),sQuery(id+"F0.wireOp",EDGE,"E155")])],"isStart":false});
            var sketch = newSketch(context, id + "F17", { "sketchPlane" : qUnion([Q0])});
            skSolve(sketch);
        }
        {
            var Q0;
            Q0=makeQuery(id+"F1.opExtrude","SWEPT_FACE",FACE,{"disambiguationData":[OSD([sQuery(id+"F0.wireOp",EDGE,"E12")])]});
            var sketch = newSketch(context, id + "F18", { "sketchPlane" : qUnion([Q0])});
            skLineSegment(sketch, "E213", {"start": v(1218.11, 254) * mm, "end": v(1268.91, 254) * mm});
            skLineSegment(sketch, "E214", {"start": v(1268.91, 254) * mm, "end": v(1675.31, 254) * mm});
            skLineSegment(sketch, "E215", {"start": v(1675.31, 254) * mm, "end": v(1730.4, 254) * mm});
            skLineSegment(sketch, "E216", {"start": v(1730.4, 254) * mm, "end": v(2009.8, 254) * mm});
            skLineSegment(sketch, "E217", {"start": v(2009.8, 254) * mm, "end": v(2589.71, 254) * mm});
            skLineSegment(sketch, "E218", {"start": v(1472.11, 254) * mm, "end": v(1472.11, 203.2) * mm});
            skLineSegment(sketch, "E219", {"start": v(1472.11, 203.2) * mm, "end": v(1370.51, 203.2) * mm});
            skLineSegment(sketch, "E220", {"start": v(1370.51, 203.2) * mm, "end": v(1370.51, 101.6) * mm});
            skLineSegment(sketch, "E221", {"start": v(1370.51, 101.6) * mm, "end": v(1573.71, 101.6) * mm});
            skLineSegment(sketch, "E222", {"start": v(1573.71, 101.6) * mm, "end": v(1573.71, 203.2) * mm});
            skLineSegment(sketch, "E223", {"start": v(1573.71, 203.2) * mm, "end": v(1472.11, 203.2) * mm});
            skLineSegment(sketch, "E224", {"start": v(2299.75, 254) * mm, "end": v(2299.75, 203.2) * mm});
            skLineSegment(sketch, "E225", {"start": v(2299.75, 203.2) * mm, "end": v(2147.35, 203.2) * mm});
            skLineSegment(sketch, "E226", {"start": v(2147.35, 203.2) * mm, "end": v(2147.35, 101.6) * mm});
            skLineSegment(sketch, "E227", {"start": v(2147.35, 101.6) * mm, "end": v(2452.15, 101.6) * mm});
            skLineSegment(sketch, "E228", {"start": v(2452.15, 101.6) * mm, "end": v(2452.15, 203.2) * mm});
            skLineSegment(sketch, "E229", {"start": v(2452.15, 203.2) * mm, "end": v(2299.75, 203.2) * mm});
            skSolve(sketch);
        }
        {
            var Q0;
            Q0=qSketchRegion(id+"F18",true);
            extrude(context, id + "F19", {"entities" : qUnion([Q0]), "operationType" : NewBodyOperationType.REMOVE, "oppositeDirection" : true, "depth" : 76.2 * mm, "offsetDistance" : 25.4 * mm});
        }
        {
            var Q0;
            Q0=makeQuery(id+"F1.opExtrude","SWEPT_FACE",FACE,{"disambiguationData":[OSD([sQuery(id+"F0.wireOp",EDGE,"E13"),sQuery(id+"F0.wireOp",EDGE,"E106"),sQuery(id+"F0.wireOp",EDGE,"E108"),sQuery(id+"F0.wireOp",EDGE,"E125")])]});
            var sketch = newSketch(context, id + "F20", { "sketchPlane" : qUnion([Q0])});
            skLineSegment(sketch, "E230", {"start": v(-2136.53, 254) * mm, "end": v(-2085.73, 254) * mm});
            skLineSegment(sketch, "E231", {"start": v(-2085.73, 254) * mm, "end": v(-1399.93, 254) * mm});
            skLineSegment(sketch, "E232", {"start": v(-1399.93, 254) * mm, "end": v(-1349.13, 254) * mm});
            skLineSegment(sketch, "E233", {"start": v(-1742.83, 254) * mm, "end": v(-1742.83, 203.2) * mm});
            skLineSegment(sketch, "E234", {"start": v(-1742.83, 203.2) * mm, "end": v(-1920.63, 203.2) * mm});
            skLineSegment(sketch, "E235", {"start": v(-1920.63, 203.2) * mm, "end": v(-1920.63, 76.2) * mm});
            skLineSegment(sketch, "E236", {"start": v(-1920.63, 76.2) * mm, "end": v(-1565.03, 76.2) * mm});
            skLineSegment(sketch, "E237", {"start": v(-1565.03, 76.2) * mm, "end": v(-1565.03, 203.2) * mm});
            skLineSegment(sketch, "E238", {"start": v(-1565.03, 203.2) * mm, "end": v(-1742.83, 203.2) * mm});
            skSolve(sketch);
        }
        {
            var Q0;
            Q0=qSketchRegion(id+"F20",true);
            extrude(context, id + "F21", {"entities" : qUnion([Q0]), "operationType" : NewBodyOperationType.REMOVE, "oppositeDirection" : true, "depth" : 76.2 * mm, "offsetDistance" : 25.4 * mm});
        }
        {
            var Q0;
            Q0=makeQuery(id+"F1.opExtrude","SWEPT_FACE",FACE,{"disambiguationData":[OSD([sQuery(id+"F0.wireOp",EDGE,"E13"),sQuery(id+"F0.wireOp",EDGE,"E106"),sQuery(id+"F0.wireOp",EDGE,"E108"),sQuery(id+"F0.wireOp",EDGE,"E125")])]});
            var sketch = newSketch(context, id + "F22", { "sketchPlane" : qUnion([Q0])});
            skLineSegment(sketch, "E239", {"start": v(-231.53, 254) * mm, "end": v(-282.33, 254) * mm});
            skLineSegment(sketch, "E240", {"start": v(-282.33, 254) * mm, "end": v(-1323.73, 254) * mm});
            skLineSegment(sketch, "E241", {"start": v(-803.03, 254) * mm, "end": v(-803.03, 203.2) * mm});
            skPoint(sketch, "E241.endSnap0", {"position": v(-803.03, 254) * mm});
            skLineSegment(sketch, "E242", {"start": v(-803.03, 203.2) * mm, "end": v(-1285.63, 203.2) * mm});
            skLineSegment(sketch, "E243", {"start": v(-1285.63, 203.2) * mm, "end": v(-1285.63, 25.4) * mm});
            skLineSegment(sketch, "E244", {"start": v(-1285.63, 25.4) * mm, "end": v(-320.43, 25.4) * mm});
            skLineSegment(sketch, "E245", {"start": v(-320.43, 25.4) * mm, "end": v(-320.43, 203.2) * mm});
            skLineSegment(sketch, "E246", {"start": v(-320.43, 203.2) * mm, "end": v(-803.03, 203.2) * mm});
            skSolve(sketch);
        }
        {
            var Q0;
            Q0=qSketchRegion(id+"F22",true);
            extrude(context, id + "F23", {"entities" : qUnion([Q0]), "operationType" : NewBodyOperationType.REMOVE, "oppositeDirection" : true, "depth" : 76.2 * mm, "offsetDistance" : 25.4 * mm});
        }
        {
            var Q0;
            Q0=makeQuery(id+"F1.opExtrude","SWEPT_FACE",FACE,{"disambiguationData":[OSD([sQuery(id+"F0.wireOp",EDGE,"E22"),sQuery(id+"F0.wireOp",EDGE,"E107")])]});
            var sketch = newSketch(context, id + "F24", { "sketchPlane" : qUnion([Q0])});
            skLineSegment(sketch, "E247", {"start": v(-2589.71, 254) * mm, "end": v(-2538.91, 254) * mm});
            skLineSegment(sketch, "E248", {"start": v(-2538.91, 203.2) * mm, "end": v(-2538.91, 25.4) * mm});
            skLineSegment(sketch, "E249", {"start": v(-2538.91, 254) * mm, "end": v(-2081.71, 254) * mm});
            skLineSegment(sketch, "E250", {"start": v(-2081.71, 25.4) * mm, "end": v(-2538.91, 25.4) * mm});
            skLineSegment(sketch, "E251", {"start": v(-2081.71, 25.4) * mm, "end": v(-2081.71, 203.2) * mm});
            skLineSegment(sketch, "E252", {"start": v(-2081.71, 203.2) * mm, "end": v(-2538.91, 203.2) * mm});
            skSolve(sketch);
        }
        {
            var Q0;
            Q0=qSketchRegion(id+"F24",true);
            extrude(context, id + "F25", {"entities" : qUnion([Q0]), "operationType" : NewBodyOperationType.REMOVE, "oppositeDirection" : true, "depth" : 76.2 * mm, "offsetDistance" : 25.4 * mm});
        }
        {
            var Q0;
            Q0=makeQuery(id+"F1.opExtrude","SWEPT_FACE",FACE,{"disambiguationData":[OSD([sQuery(id+"F0.wireOp",EDGE,"E22"),sQuery(id+"F0.wireOp",EDGE,"E107")])]});
            var sketch = newSketch(context, id + "F26", { "sketchPlane" : qUnion([Q0])});
            skLineSegment(sketch, "E253", {"start": v(-2081.71, 203.2) * mm, "end": v(-1980.11, 203.2) * mm});
            skLineSegment(sketch, "E254", {"start": v(-1980.11, 203.2) * mm, "end": v(-1294.31, 203.2) * mm});
            skLineSegment(sketch, "E255", {"start": v(-1637.21, 76.2) * mm, "end": v(-1764.21, 76.2) * mm});
            skLineSegment(sketch, "E256", {"start": v(-1764.21, 76.2) * mm, "end": v(-1764.21, 203.2) * mm});
            skLineSegment(sketch, "E257", {"start": v(-1764.21, 203.2) * mm, "end": v(-1510.21, 203.2) * mm});
            skLineSegment(sketch, "E258", {"start": v(-1510.21, 203.2) * mm, "end": v(-1510.21, 76.2) * mm});
            skLineSegment(sketch, "E259", {"start": v(-1510.21, 76.2) * mm, "end": v(-1637.21, 76.2) * mm});
            skSolve(sketch);
        }
        {
            var Q0;
            Q0=makeQuery(id+"F26.imprint","IMPRINT",FACE,{"disambiguationData":[TD([[makeQuery(id+"F26.imprint","IMPRINT",EDGE,{"derivedFrom":sQuery(id+"F26.wireOp",EDGE,"E255")}),-1.0]])]});
            extrude(context, id + "F27", {"entities" : qUnion([Q0]), "operationType" : NewBodyOperationType.REMOVE, "oppositeDirection" : true, "depth" : 76.2 * mm, "offsetDistance" : 25.4 * mm});
        }
        {
            var Q0;
            Q0=makeQuery(id+"F1.opExtrude","SWEPT_FACE",FACE,{"disambiguationData":[OSD([sQuery(id+"F0.wireOp",EDGE,"E22"),sQuery(id+"F0.wireOp",EDGE,"E107")])]});
            var sketch = newSketch(context, id + "F28", { "sketchPlane" : qUnion([Q0])});
            skLineSegment(sketch, "E260", {"start": v(-2538.91, 203.2) * mm, "end": v(-2081.71, 203.2) * mm});
            skLineSegment(sketch, "E261", {"start": v(-2310.31, 25.4) * mm, "end": v(-2361.11, 25.4) * mm});
            skLineSegment(sketch, "E262", {"start": v(-2361.11, 25.4) * mm, "end": v(-2361.11, 203.2) * mm});
            skLineSegment(sketch, "E263", {"start": v(-2361.11, 203.2) * mm, "end": v(-2310.31, 203.2) * mm});
            skLineSegment(sketch, "E264", {"start": v(-2310.31, 203.2) * mm, "end": v(-2259.51, 203.2) * mm});
            skLineSegment(sketch, "E265", {"start": v(-2259.51, 203.2) * mm, "end": v(-2259.51, 25.4) * mm});
            skLineSegment(sketch, "E266", {"start": v(-2259.51, 25.4) * mm, "end": v(-2310.31, 25.4) * mm});
            skLineSegment(sketch, "E267", {"start": v(-2361.11, 203.2) * mm, "end": v(-2361.11, 254) * mm});
            skLineSegment(sketch, "E268", {"start": v(-2361.11, 254) * mm, "end": v(-2259.51, 254) * mm});
            skLineSegment(sketch, "E269", {"start": v(-2259.51, 254) * mm, "end": v(-2259.51, 203.2) * mm});
            skLineSegment(sketch, "E270", {"start": v(-2361.11, 254) * mm, "end": v(-2386.51, 254) * mm});
            skLineSegment(sketch, "E271", {"start": v(-2386.51, 254) * mm, "end": v(-2386.51, 0) * mm});
            skLineSegment(sketch, "E272", {"start": v(-2386.51, 0) * mm, "end": v(-2259.51, 0) * mm});
            skLineSegment(sketch, "E273", {"start": v(-2259.51, 0) * mm, "end": v(-2259.51, 25.4) * mm});
            skLineSegment(sketch, "E274", {"start": v(-2259.51, 0) * mm, "end": v(-2234.11, 0) * mm});
            skLineSegment(sketch, "E275", {"start": v(-2234.11, 0) * mm, "end": v(-2234.11, 254) * mm});
            skLineSegment(sketch, "E276", {"start": v(-2234.11, 254) * mm, "end": v(-2259.51, 254) * mm});
            skLineSegment(sketch, "E277", {"start": v(-2386.51, 254) * mm, "end": v(-2234.11, 254) * mm});
            skSolve(sketch);
        }
        {
            var Q0;
            {var subQ1=sQuery(id+"F28.wireOp",EDGE,"E261");var subQ9=sQuery(id+"F28.wireOp",EDGE,"E262");var subQ11=sQuery(id+"F28.wireOp",EDGE,"E273");var subQ12=makeQuery(id+"F28.imprint","IMPRINT",EDGE,{"derivedFrom":subQ11});var subQ13=sQuery(id+"F28.wireOp",EDGE,"E267");var subQ18=makeQuery(id+"F28.imprint","IMPRINT",EDGE,{"derivedFrom":subQ13});var subQ22=sQuery(id+"F28.wireOp",EDGE,"E269");var subQ23=sQuery(id+"F28.wireOp",EDGE,"E265");var subQ25=makeQuery(id+"F28.imprint","IMPRINT",EDGE,{"derivedFrom":subQ22});Q0=qUnion([makeQuery(id+"F28.imprint","IMPRINT",FACE,{"disambiguationData":[TD([[subQ12,-1.0]])]}),makeQuery(id+"F28.imprint","IMPRINT",FACE,{"disambiguationData":[TD([[subQ25,1.0]])]}),makeQuery(id+"F28.imprint","IMPRINT",FACE,{"disambiguationData":[TD([[makeQuery(id+"F28.imprint","IMPRINT",EDGE,{"derivedFrom":subQ23}),1.0]])]}),makeQuery(id+"F28.imprint","IMPRINT",FACE,{"disambiguationData":[TD([[subQ18,-1.0]])]}),makeQuery(id+"F28.imprint","IMPRINT",FACE,{"disambiguationData":[TD([[makeQuery(id+"F28.imprint","IMPRINT",EDGE,{"derivedFrom":subQ9}),1.0]])]}),makeQuery(id+"F28.imprint","IMPRINT",FACE,{"disambiguationData":[TD([[subQ18,1.0]])]}),makeQuery(id+"F28.imprint","IMPRINT",FACE,{"disambiguationData":[TD([[makeQuery(id+"F28.imprint","IMPRINT",EDGE,{"derivedFrom":subQ1}),1.0]])]})]);}
            extrude(context, id + "F29", {"entities" : qUnion([Q0]), "oppositeDirection" : true, "depth" : 50.8 * mm, "offsetDistance" : 25.4 * mm});
        }
        {
            var Q0;
            Q0=makeQuery(id+"F1.opExtrude","CAP_FACE",FACE,{"disambiguationData":[OSD([sQuery(id+"F0.wireOp",EDGE,"E0"),sQuery(id+"F0.wireOp",EDGE,"E1"),sQuery(id+"F0.wireOp",EDGE,"E2"),sQuery(id+"F0.wireOp",EDGE,"E3"),sQuery(id+"F0.wireOp",EDGE,"E4"),sQuery(id+"F0.wireOp",EDGE,"E5"),sQuery(id+"F0.wireOp",EDGE,"E6"),sQuery(id+"F0.wireOp",EDGE,"E7"),sQuery(id+"F0.wireOp",EDGE,"E8"),sQuery(id+"F0.wireOp",EDGE,"E9"),sQuery(id+"F0.wireOp",EDGE,"E10"),sQuery(id+"F0.wireOp",EDGE,"E11"),sQuery(id+"F0.wireOp",EDGE,"E12"),sQuery(id+"F0.wireOp",EDGE,"E13"),sQuery(id+"F0.wireOp",EDGE,"E14"),sQuery(id+"F0.wireOp",EDGE,"E15"),sQuery(id+"F0.wireOp",EDGE,"E16"),sQuery(id+"F0.wireOp",EDGE,"E17"),sQuery(id+"F0.wireOp",EDGE,"E18"),sQuery(id+"F0.wireOp",EDGE,"E19"),sQuery(id+"F0.wireOp",EDGE,"E20"),sQuery(id+"F0.wireOp",EDGE,"E21"),sQuery(id+"F0.wireOp",EDGE,"E22"),sQuery(id+"F0.wireOp",EDGE,"E23"),sQuery(id+"F0.wireOp",EDGE,"E24"),sQuery(id+"F0.wireOp",EDGE,"E25"),sQuery(id+"F0.wireOp",EDGE,"E26"),sQuery(id+"F0.wireOp",EDGE,"E27"),sQuery(id+"F0.wireOp",EDGE,"E28"),sQuery(id+"F0.wireOp",EDGE,"E29"),sQuery(id+"F0.wireOp",EDGE,"E30"),sQuery(id+"F0.wireOp",EDGE,"E31"),sQuery(id+"F0.wireOp",EDGE,"E32"),sQuery(id+"F0.wireOp",EDGE,"E34"),sQuery(id+"F0.wireOp",EDGE,"E35"),sQuery(id+"F0.wireOp",EDGE,"E36"),sQuery(id+"F0.wireOp",EDGE,"E37"),sQuery(id+"F0.wireOp",EDGE,"E38"),sQuery(id+"F0.wireOp",EDGE,"E39"),sQuery(id+"F0.wireOp",EDGE,"E40"),sQuery(id+"F0.wireOp",EDGE,"E41"),sQuery(id+"F0.wireOp",EDGE,"E42"),sQuery(id+"F0.wireOp",EDGE,"E43"),sQuery(id+"F0.wireOp",EDGE,"E44"),sQuery(id+"F0.wireOp",EDGE,"E45"),sQuery(id+"F0.wireOp",EDGE,"E46"),sQuery(id+"F0.wireOp",EDGE,"E47"),sQuery(id+"F0.wireOp",EDGE,"E48"),sQuery(id+"F0.wireOp",EDGE,"E49"),sQuery(id+"F0.wireOp",EDGE,"E50"),sQuery(id+"F0.wireOp",EDGE,"E51"),sQuery(id+"F0.wireOp",EDGE,"E52"),sQuery(id+"F0.wireOp",EDGE,"E53"),sQuery(id+"F0.wireOp",EDGE,"E54"),sQuery(id+"F0.wireOp",EDGE,"E55"),sQuery(id+"F0.wireOp",EDGE,"E56"),sQuery(id+"F0.wireOp",EDGE,"E57"),sQuery(id+"F0.wireOp",EDGE,"E58"),sQuery(id+"F0.wireOp",EDGE,"E59"),sQuery(id+"F0.wireOp",EDGE,"E60"),sQuery(id+"F0.wireOp",EDGE,"E61"),sQuery(id+"F0.wireOp",EDGE,"E62"),sQuery(id+"F0.wireOp",EDGE,"E63"),sQuery(id+"F0.wireOp",EDGE,"E64"),sQuery(id+"F0.wireOp",EDGE,"E65"),sQuery(id+"F0.wireOp",EDGE,"E66"),sQuery(id+"F0.wireOp",EDGE,"E67"),sQuery(id+"F0.wireOp",EDGE,"E68"),sQuery(id+"F0.wireOp",EDGE,"E69"),sQuery(id+"F0.wireOp",EDGE,"E70"),sQuery(id+"F0.wireOp",EDGE,"E71"),sQuery(id+"F0.wireOp",EDGE,"E72"),sQuery(id+"F0.wireOp",EDGE,"E73"),sQuery(id+"F0.wireOp",EDGE,"E74"),sQuery(id+"F0.wireOp",EDGE,"E75"),sQuery(id+"F0.wireOp",EDGE,"E76"),sQuery(id+"F0.wireOp",EDGE,"E77"),sQuery(id+"F0.wireOp",EDGE,"E78"),sQuery(id+"F0.wireOp",EDGE,"E79"),sQuery(id+"F0.wireOp",EDGE,"E80"),sQuery(id+"F0.wireOp",EDGE,"E81"),sQuery(id+"F0.wireOp",EDGE,"E82"),sQuery(id+"F0.wireOp",EDGE,"E83"),sQuery(id+"F0.wireOp",EDGE,"E84"),sQuery(id+"F0.wireOp",EDGE,"E85"),sQuery(id+"F0.wireOp",EDGE,"E86"),sQuery(id+"F0.wireOp",EDGE,"E87"),sQuery(id+"F0.wireOp",EDGE,"E88"),sQuery(id+"F0.wireOp",EDGE,"E89"),sQuery(id+"F0.wireOp",EDGE,"E90"),sQuery(id+"F0.wireOp",EDGE,"E91"),sQuery(id+"F0.wireOp",EDGE,"E92"),sQuery(id+"F0.wireOp",EDGE,"E93"),sQuery(id+"F0.wireOp",EDGE,"E94"),sQuery(id+"F0.wireOp",EDGE,"E95"),sQuery(id+"F0.wireOp",EDGE,"E96"),sQuery(id+"F0.wireOp",EDGE,"E97"),sQuery(id+"F0.wireOp",EDGE,"E98"),sQuery(id+"F0.wireOp",EDGE,"E99"),sQuery(id+"F0.wireOp",EDGE,"E100"),sQuery(id+"F0.wireOp",EDGE,"E101"),sQuery(id+"F0.wireOp",EDGE,"E102"),sQuery(id+"F0.wireOp",EDGE,"E103"),sQuery(id+"F0.wireOp",EDGE,"E104"),sQuery(id+"F0.wireOp",EDGE,"E105"),sQuery(id+"F0.wireOp",EDGE,"E106"),sQuery(id+"F0.wireOp",EDGE,"E107"),sQuery(id+"F0.wireOp",EDGE,"E108"),sQuery(id+"F0.wireOp",EDGE,"E109"),sQuery(id+"F0.wireOp",EDGE,"E110"),sQuery(id+"F0.wireOp",EDGE,"E111"),sQuery(id+"F0.wireOp",EDGE,"E112"),sQuery(id+"F0.wireOp",EDGE,"E113"),sQuery(id+"F0.wireOp",EDGE,"E114"),sQuery(id+"F0.wireOp",EDGE,"E115"),sQuery(id+"F0.wireOp",EDGE,"E116"),sQuery(id+"F0.wireOp",EDGE,"E117"),sQuery(id+"F0.wireOp",EDGE,"E118"),sQuery(id+"F0.wireOp",EDGE,"E119"),sQuery(id+"F0.wireOp",EDGE,"E120"),sQuery(id+"F0.wireOp",EDGE,"E121"),sQuery(id+"F0.wireOp",EDGE,"E122"),sQuery(id+"F0.wireOp",EDGE,"E123"),sQuery(id+"F0.wireOp",EDGE,"E124"),sQuery(id+"F0.wireOp",EDGE,"E125"),sQuery(id+"F0.wireOp",EDGE,"E126"),sQuery(id+"F0.wireOp",EDGE,"E127"),sQuery(id+"F0.wireOp",EDGE,"E128"),sQuery(id+"F0.wireOp",EDGE,"E129"),sQuery(id+"F0.wireOp",EDGE,"E130"),sQuery(id+"F0.wireOp",EDGE,"E131"),sQuery(id+"F0.wireOp",EDGE,"E132"),sQuery(id+"F0.wireOp",EDGE,"E133"),sQuery(id+"F0.wireOp",EDGE,"E137"),sQuery(id+"F0.wireOp",EDGE,"E141"),sQuery(id+"F0.wireOp",EDGE,"E142"),sQuery(id+"F0.wireOp",EDGE,"E143"),sQuery(id+"F0.wireOp",EDGE,"E146"),sQuery(id+"F0.wireOp",EDGE,"E147"),sQuery(id+"F0.wireOp",EDGE,"E148"),sQuery(id+"F0.wireOp",EDGE,"E151"),sQuery(id+"F0.wireOp",EDGE,"E152"),sQuery(id+"F0.wireOp",EDGE,"E153"),sQuery(id+"F0.wireOp",EDGE,"E154"),sQuery(id+"F0.wireOp",EDGE,"E155"),sQuery(id+"F0.wireOp",EDGE,"E156"),sQuery(id+"F0.wireOp",EDGE,"E157"),sQuery(id+"F0.wireOp",EDGE,"E158"),sQuery(id+"F0.wireOp",EDGE,"E159"),sQuery(id+"F0.wireOp",EDGE,"E160"),sQuery(id+"F0.wireOp",EDGE,"E161"),sQuery(id+"F0.wireOp",EDGE,"E162"),sQuery(id+"F0.wireOp",EDGE,"E163"),sQuery(id+"F0.wireOp",EDGE,"E164"),sQuery(id+"F0.wireOp",EDGE,"E165"),sQuery(id+"F0.wireOp",EDGE,"E166"),sQuery(id+"F0.wireOp",EDGE,"E167"),sQuery(id+"F0.wireOp",EDGE,"E168")])],"isStart":true});
            var sketch = newSketch(context, id + "F30", { "sketchPlane" : qUnion([Q0])});
            skLineSegment(sketch, "E278.bottom", {"start": v(-1104.75, 597.15) * mm, "end": v(2950.43, 597.15) * mm});
            skLineSegment(sketch, "E278.top", {"start": v(-1104.75, -3137.36) * mm, "end": v(2950.43, -3137.36) * mm});
            skLineSegment(sketch, "E278.left", {"start": v(-1104.75, 597.15) * mm, "end": v(-1104.75, -3137.36) * mm});
            skLineSegment(sketch, "E278.right", {"start": v(2950.43, 597.15) * mm, "end": v(2950.43, -3137.36) * mm});
            skSolve(sketch);
        }
        {
            var Q0;
            Q0=makeQuery(id+"F30.imprint","IMPRINT",FACE,{"disambiguationData":[TD([[makeQuery(id+"F30.imprint","IMPRINT",EDGE,{"derivedFrom":sQuery(id+"F30.wireOp",EDGE,"E278.bottom")}),-1.0]])]});
            var Q1;
            Q1=makeQuery(id+"F30.imprint","IMPRINT",FACE,{"disambiguationData":[TD([[makeQuery(id+"F30.imprint","IMPRINT",EDGE,{"derivedFrom":makeQuery(id+"F1.opExtrude","CAP_EDGE",EDGE,{"disambiguationData":[OSD([sQuery(id+"F0.wireOp",EDGE,"E16")])],"isStart":true})}),-1.0]])]});
            extrude(context, id + "F31", {"entities" : qUnion([Q0, Q1]), "depth" : 50.8 * mm, "offsetDistance" : 25.4 * mm});
        }
        {
            var Q0;
            Q0=makeQuery(id+"F31.opExtrude","CAP_FACE",FACE,{"disambiguationData":[OSD([sQuery(id+"F0.wireOp",EDGE,"E1"),sQuery(id+"F0.wireOp",EDGE,"E2"),sQuery(id+"F0.wireOp",EDGE,"E3"),sQuery(id+"F0.wireOp",EDGE,"E4"),sQuery(id+"F0.wireOp",EDGE,"E6"),sQuery(id+"F0.wireOp",EDGE,"E7"),sQuery(id+"F0.wireOp",EDGE,"E8"),sQuery(id+"F0.wireOp",EDGE,"E9"),sQuery(id+"F0.wireOp",EDGE,"E10"),sQuery(id+"F0.wireOp",EDGE,"E11"),sQuery(id+"F0.wireOp",EDGE,"E12"),sQuery(id+"F0.wireOp",EDGE,"E13"),sQuery(id+"F0.wireOp",EDGE,"E19"),sQuery(id+"F0.wireOp",EDGE,"E20"),sQuery(id+"F0.wireOp",EDGE,"E21"),sQuery(id+"F0.wireOp",EDGE,"E22"),sQuery(id+"F0.wireOp",EDGE,"E24"),sQuery(id+"F0.wireOp",EDGE,"E25"),sQuery(id+"F0.wireOp",EDGE,"E26"),sQuery(id+"F0.wireOp",EDGE,"E27"),sQuery(id+"F0.wireOp",EDGE,"E28"),sQuery(id+"F0.wireOp",EDGE,"E29"),sQuery(id+"F0.wireOp",EDGE,"E30"),sQuery(id+"F0.wireOp",EDGE,"E31"),sQuery(id+"F0.wireOp",EDGE,"E32"),sQuery(id+"F0.wireOp",EDGE,"E34"),sQuery(id+"F0.wireOp",EDGE,"E35"),sQuery(id+"F0.wireOp",EDGE,"E36"),sQuery(id+"F0.wireOp",EDGE,"E37"),sQuery(id+"F0.wireOp",EDGE,"E38"),sQuery(id+"F0.wireOp",EDGE,"E39"),sQuery(id+"F0.wireOp",EDGE,"E40"),sQuery(id+"F0.wireOp",EDGE,"E41"),sQuery(id+"F0.wireOp",EDGE,"E42"),sQuery(id+"F0.wireOp",EDGE,"E43"),sQuery(id+"F0.wireOp",EDGE,"E44"),sQuery(id+"F0.wireOp",EDGE,"E45"),sQuery(id+"F0.wireOp",EDGE,"E46"),sQuery(id+"F0.wireOp",EDGE,"E47"),sQuery(id+"F0.wireOp",EDGE,"E48"),sQuery(id+"F0.wireOp",EDGE,"E49"),sQuery(id+"F0.wireOp",EDGE,"E50"),sQuery(id+"F0.wireOp",EDGE,"E51"),sQuery(id+"F0.wireOp",EDGE,"E52"),sQuery(id+"F0.wireOp",EDGE,"E53"),sQuery(id+"F0.wireOp",EDGE,"E54"),sQuery(id+"F0.wireOp",EDGE,"E55"),sQuery(id+"F0.wireOp",EDGE,"E56"),sQuery(id+"F0.wireOp",EDGE,"E57"),sQuery(id+"F0.wireOp",EDGE,"E58"),sQuery(id+"F0.wireOp",EDGE,"E59"),sQuery(id+"F0.wireOp",EDGE,"E60"),sQuery(id+"F0.wireOp",EDGE,"E61"),sQuery(id+"F0.wireOp",EDGE,"E62"),sQuery(id+"F0.wireOp",EDGE,"E63"),sQuery(id+"F0.wireOp",EDGE,"E64"),sQuery(id+"F0.wireOp",EDGE,"E65"),sQuery(id+"F0.wireOp",EDGE,"E66"),sQuery(id+"F0.wireOp",EDGE,"E67"),sQuery(id+"F0.wireOp",EDGE,"E68"),sQuery(id+"F0.wireOp",EDGE,"E69"),sQuery(id+"F0.wireOp",EDGE,"E70"),sQuery(id+"F0.wireOp",EDGE,"E71"),sQuery(id+"F0.wireOp",EDGE,"E72"),sQuery(id+"F0.wireOp",EDGE,"E73"),sQuery(id+"F0.wireOp",EDGE,"E74"),sQuery(id+"F0.wireOp",EDGE,"E75"),sQuery(id+"F0.wireOp",EDGE,"E76"),sQuery(id+"F0.wireOp",EDGE,"E77"),sQuery(id+"F0.wireOp",EDGE,"E78"),sQuery(id+"F0.wireOp",EDGE,"E79"),sQuery(id+"F0.wireOp",EDGE,"E80"),sQuery(id+"F0.wireOp",EDGE,"E81"),sQuery(id+"F0.wireOp",EDGE,"E82"),sQuery(id+"F0.wireOp",EDGE,"E83"),sQuery(id+"F0.wireOp",EDGE,"E84"),sQuery(id+"F0.wireOp",EDGE,"E85"),sQuery(id+"F0.wireOp",EDGE,"E86"),sQuery(id+"F0.wireOp",EDGE,"E87"),sQuery(id+"F0.wireOp",EDGE,"E88"),sQuery(id+"F0.wireOp",EDGE,"E89"),sQuery(id+"F0.wireOp",EDGE,"E90"),sQuery(id+"F0.wireOp",EDGE,"E91"),sQuery(id+"F0.wireOp",EDGE,"E94"),sQuery(id+"F0.wireOp",EDGE,"E95"),sQuery(id+"F0.wireOp",EDGE,"E98"),sQuery(id+"F0.wireOp",EDGE,"E99"),sQuery(id+"F0.wireOp",EDGE,"E100"),sQuery(id+"F0.wireOp",EDGE,"E101"),sQuery(id+"F0.wireOp",EDGE,"E102"),sQuery(id+"F0.wireOp",EDGE,"E103"),sQuery(id+"F0.wireOp",EDGE,"E104"),sQuery(id+"F0.wireOp",EDGE,"E105"),sQuery(id+"F0.wireOp",EDGE,"E106"),sQuery(id+"F0.wireOp",EDGE,"E107"),sQuery(id+"F0.wireOp",EDGE,"E108"),sQuery(id+"F0.wireOp",EDGE,"E109"),sQuery(id+"F0.wireOp",EDGE,"E110"),sQuery(id+"F0.wireOp",EDGE,"E111"),sQuery(id+"F0.wireOp",EDGE,"E112"),sQuery(id+"F0.wireOp",EDGE,"E113"),sQuery(id+"F0.wireOp",EDGE,"E114"),sQuery(id+"F0.wireOp",EDGE,"E115"),sQuery(id+"F0.wireOp",EDGE,"E116"),sQuery(id+"F0.wireOp",EDGE,"E117"),sQuery(id+"F0.wireOp",EDGE,"E118"),sQuery(id+"F0.wireOp",EDGE,"E119"),sQuery(id+"F0.wireOp",EDGE,"E120"),sQuery(id+"F0.wireOp",EDGE,"E121"),sQuery(id+"F0.wireOp",EDGE,"E122"),sQuery(id+"F0.wireOp",EDGE,"E123"),sQuery(id+"F0.wireOp",EDGE,"E124"),sQuery(id+"F0.wireOp",EDGE,"E125"),sQuery(id+"F0.wireOp",EDGE,"E126"),sQuery(id+"F0.wireOp",EDGE,"E127"),sQuery(id+"F0.wireOp",EDGE,"E128"),sQuery(id+"F0.wireOp",EDGE,"E129"),sQuery(id+"F0.wireOp",EDGE,"E130"),sQuery(id+"F0.wireOp",EDGE,"E131"),sQuery(id+"F0.wireOp",EDGE,"E132"),sQuery(id+"F0.wireOp",EDGE,"E133"),sQuery(id+"F0.wireOp",EDGE,"E137"),sQuery(id+"F0.wireOp",EDGE,"E141"),sQuery(id+"F0.wireOp",EDGE,"E142"),sQuery(id+"F0.wireOp",EDGE,"E143"),sQuery(id+"F0.wireOp",EDGE,"E146"),sQuery(id+"F0.wireOp",EDGE,"E147"),sQuery(id+"F0.wireOp",EDGE,"E148"),sQuery(id+"F0.wireOp",EDGE,"E151"),sQuery(id+"F0.wireOp",EDGE,"E152"),sQuery(id+"F0.wireOp",EDGE,"E153"),sQuery(id+"F0.wireOp",EDGE,"E154"),sQuery(id+"F0.wireOp",EDGE,"E155"),sQuery(id+"F0.wireOp",EDGE,"E156"),sQuery(id+"F0.wireOp",EDGE,"E157"),sQuery(id+"F0.wireOp",EDGE,"E158"),sQuery(id+"F0.wireOp",EDGE,"E159"),sQuery(id+"F0.wireOp",EDGE,"E160"),sQuery(id+"F0.wireOp",EDGE,"E161"),sQuery(id+"F0.wireOp",EDGE,"E162"),sQuery(id+"F0.wireOp",EDGE,"E163"),sQuery(id+"F0.wireOp",EDGE,"E164"),sQuery(id+"F0.wireOp",EDGE,"E165"),sQuery(id+"F0.wireOp",EDGE,"E166"),sQuery(id+"F0.wireOp",EDGE,"E167"),sQuery(id+"F0.wireOp",EDGE,"E168"),sQuery(id+"F7.wireOp",EDGE,"E178"),sQuery(id+"F7.wireOp",EDGE,"E180"),sQuery(id+"F7.wireOp",EDGE,"E181"),sQuery(id+"F30.wireOp",EDGE,"E278.bottom"),sQuery(id+"F30.wireOp",EDGE,"E278.top"),sQuery(id+"F30.wireOp",EDGE,"E278.left"),sQuery(id+"F30.wireOp",EDGE,"E278.right")])],"isStart":true});
            var sketch = newSketch(context, id + "F32", { "sketchPlane" : qUnion([Q0])});
            skLineSegment(sketch, "E279", {"start": v(-1104.75, 3137.36) * mm, "end": v(-977.75, 3137.36) * mm});
            skLineSegment(sketch, "E280", {"start": v(-977.75, 3137.36) * mm, "end": v(-977.75, -672.64) * mm});
            skLineSegment(sketch, "E281", {"start": v(-977.75, -672.64) * mm, "end": v(2832.25, -672.64) * mm});
            skLineSegment(sketch, "E282", {"start": v(2832.25, -672.64) * mm, "end": v(2832.25, 2807.16) * mm});
            skLineSegment(sketch, "E283", {"start": v(2832.25, 2807.16) * mm, "end": v(-977.75, 2807.16) * mm});
            skLineSegment(sketch, "E284", {"start": v(-977.75, 3137.36) * mm, "end": v(2950.43, 3137.36) * mm});
            skLineSegment(sketch, "E285", {"start": v(2950.43, 3137.36) * mm, "end": v(2950.43, -597.15) * mm});
            skLineSegment(sketch, "E286", {"start": v(2950.43, -597.15) * mm, "end": v(-1104.75, -597.15) * mm});
            skLineSegment(sketch, "E287", {"start": v(-1104.75, -597.15) * mm, "end": v(-1104.75, 3137.36) * mm});
            skSolve(sketch);
        }
        {
            var Q0;
            {var subQ81=sQuery(id+"F32.wireOp",EDGE,"E281");Q0=makeQuery(id+"F32.imprint","IMPRINT",FACE,{"disambiguationData":[TD([[makeQuery(id+"F32.imprint","IMPRINT",EDGE,{"derivedFrom":subQ81}),1.0]])]});}
            var sketch = newSketch(context, id + "F33", { "sketchPlane" : qUnion([Q0])});
            skLineSegment(sketch, "E288", {"start": v(-762, 2419.47) * mm, "end": v(-762, 1403.47) * mm});
            skLineSegment(sketch, "E289", {"start": v(-762, 1403.47) * mm, "end": v(0, 1403.47) * mm});
            skLineSegment(sketch, "E290", {"start": v(0, 1403.47) * mm, "end": v(0, 2419.47) * mm});
            skLineSegment(sketch, "E291", {"start": v(0, 2419.47) * mm, "end": v(-762, 2419.47) * mm});
            skSolve(sketch);
        }
        {
            var Q0;
            Q0=makeQuery(id+"F33.imprint","IMPRINT",FACE,{"disambiguationData":[TD([[makeQuery(id+"F33.imprint","IMPRINT",EDGE,{"derivedFrom":sQuery(id+"F33.wireOp",EDGE,"E288")}),1.0]])]});
            extrude(context, id + "F34", {"entities" : qUnion([Q0]), "operationType" : NewBodyOperationType.REMOVE, "oppositeDirection" : true, "depth" : 76.2 * mm, "offsetDistance" : 25.4 * mm});
        }
        {
            var Q0;
            Q0=makeQuery(id+"F31.opExtrude","CAP_FACE",FACE,{"disambiguationData":[OSD([sQuery(id+"F0.wireOp",EDGE,"E1"),sQuery(id+"F0.wireOp",EDGE,"E2"),sQuery(id+"F0.wireOp",EDGE,"E3"),sQuery(id+"F0.wireOp",EDGE,"E4"),sQuery(id+"F0.wireOp",EDGE,"E6"),sQuery(id+"F0.wireOp",EDGE,"E7"),sQuery(id+"F0.wireOp",EDGE,"E8"),sQuery(id+"F0.wireOp",EDGE,"E9"),sQuery(id+"F0.wireOp",EDGE,"E10"),sQuery(id+"F0.wireOp",EDGE,"E11"),sQuery(id+"F0.wireOp",EDGE,"E12"),sQuery(id+"F0.wireOp",EDGE,"E13"),sQuery(id+"F0.wireOp",EDGE,"E19"),sQuery(id+"F0.wireOp",EDGE,"E20"),sQuery(id+"F0.wireOp",EDGE,"E21"),sQuery(id+"F0.wireOp",EDGE,"E22"),sQuery(id+"F0.wireOp",EDGE,"E24"),sQuery(id+"F0.wireOp",EDGE,"E25"),sQuery(id+"F0.wireOp",EDGE,"E26"),sQuery(id+"F0.wireOp",EDGE,"E27"),sQuery(id+"F0.wireOp",EDGE,"E28"),sQuery(id+"F0.wireOp",EDGE,"E29"),sQuery(id+"F0.wireOp",EDGE,"E30"),sQuery(id+"F0.wireOp",EDGE,"E31"),sQuery(id+"F0.wireOp",EDGE,"E32"),sQuery(id+"F0.wireOp",EDGE,"E34"),sQuery(id+"F0.wireOp",EDGE,"E35"),sQuery(id+"F0.wireOp",EDGE,"E36"),sQuery(id+"F0.wireOp",EDGE,"E37"),sQuery(id+"F0.wireOp",EDGE,"E38"),sQuery(id+"F0.wireOp",EDGE,"E39"),sQuery(id+"F0.wireOp",EDGE,"E40"),sQuery(id+"F0.wireOp",EDGE,"E41"),sQuery(id+"F0.wireOp",EDGE,"E42"),sQuery(id+"F0.wireOp",EDGE,"E43"),sQuery(id+"F0.wireOp",EDGE,"E44"),sQuery(id+"F0.wireOp",EDGE,"E45"),sQuery(id+"F0.wireOp",EDGE,"E46"),sQuery(id+"F0.wireOp",EDGE,"E47"),sQuery(id+"F0.wireOp",EDGE,"E48"),sQuery(id+"F0.wireOp",EDGE,"E49"),sQuery(id+"F0.wireOp",EDGE,"E50"),sQuery(id+"F0.wireOp",EDGE,"E51"),sQuery(id+"F0.wireOp",EDGE,"E52"),sQuery(id+"F0.wireOp",EDGE,"E53"),sQuery(id+"F0.wireOp",EDGE,"E54"),sQuery(id+"F0.wireOp",EDGE,"E55"),sQuery(id+"F0.wireOp",EDGE,"E56"),sQuery(id+"F0.wireOp",EDGE,"E57"),sQuery(id+"F0.wireOp",EDGE,"E58"),sQuery(id+"F0.wireOp",EDGE,"E59"),sQuery(id+"F0.wireOp",EDGE,"E60"),sQuery(id+"F0.wireOp",EDGE,"E61"),sQuery(id+"F0.wireOp",EDGE,"E62"),sQuery(id+"F0.wireOp",EDGE,"E63"),sQuery(id+"F0.wireOp",EDGE,"E64"),sQuery(id+"F0.wireOp",EDGE,"E65"),sQuery(id+"F0.wireOp",EDGE,"E66"),sQuery(id+"F0.wireOp",EDGE,"E67"),sQuery(id+"F0.wireOp",EDGE,"E68"),sQuery(id+"F0.wireOp",EDGE,"E69"),sQuery(id+"F0.wireOp",EDGE,"E70"),sQuery(id+"F0.wireOp",EDGE,"E71"),sQuery(id+"F0.wireOp",EDGE,"E72"),sQuery(id+"F0.wireOp",EDGE,"E73"),sQuery(id+"F0.wireOp",EDGE,"E74"),sQuery(id+"F0.wireOp",EDGE,"E75"),sQuery(id+"F0.wireOp",EDGE,"E76"),sQuery(id+"F0.wireOp",EDGE,"E77"),sQuery(id+"F0.wireOp",EDGE,"E78"),sQuery(id+"F0.wireOp",EDGE,"E79"),sQuery(id+"F0.wireOp",EDGE,"E80"),sQuery(id+"F0.wireOp",EDGE,"E81"),sQuery(id+"F0.wireOp",EDGE,"E82"),sQuery(id+"F0.wireOp",EDGE,"E83"),sQuery(id+"F0.wireOp",EDGE,"E84"),sQuery(id+"F0.wireOp",EDGE,"E85"),sQuery(id+"F0.wireOp",EDGE,"E86"),sQuery(id+"F0.wireOp",EDGE,"E87"),sQuery(id+"F0.wireOp",EDGE,"E88"),sQuery(id+"F0.wireOp",EDGE,"E89"),sQuery(id+"F0.wireOp",EDGE,"E90"),sQuery(id+"F0.wireOp",EDGE,"E91"),sQuery(id+"F0.wireOp",EDGE,"E94"),sQuery(id+"F0.wireOp",EDGE,"E95"),sQuery(id+"F0.wireOp",EDGE,"E98"),sQuery(id+"F0.wireOp",EDGE,"E99"),sQuery(id+"F0.wireOp",EDGE,"E100"),sQuery(id+"F0.wireOp",EDGE,"E101"),sQuery(id+"F0.wireOp",EDGE,"E102"),sQuery(id+"F0.wireOp",EDGE,"E103"),sQuery(id+"F0.wireOp",EDGE,"E104"),sQuery(id+"F0.wireOp",EDGE,"E105"),sQuery(id+"F0.wireOp",EDGE,"E106"),sQuery(id+"F0.wireOp",EDGE,"E107"),sQuery(id+"F0.wireOp",EDGE,"E108"),sQuery(id+"F0.wireOp",EDGE,"E109"),sQuery(id+"F0.wireOp",EDGE,"E110"),sQuery(id+"F0.wireOp",EDGE,"E111"),sQuery(id+"F0.wireOp",EDGE,"E112"),sQuery(id+"F0.wireOp",EDGE,"E113"),sQuery(id+"F0.wireOp",EDGE,"E114"),sQuery(id+"F0.wireOp",EDGE,"E115"),sQuery(id+"F0.wireOp",EDGE,"E116"),sQuery(id+"F0.wireOp",EDGE,"E117"),sQuery(id+"F0.wireOp",EDGE,"E118"),sQuery(id+"F0.wireOp",EDGE,"E119"),sQuery(id+"F0.wireOp",EDGE,"E120"),sQuery(id+"F0.wireOp",EDGE,"E121"),sQuery(id+"F0.wireOp",EDGE,"E122"),sQuery(id+"F0.wireOp",EDGE,"E123"),sQuery(id+"F0.wireOp",EDGE,"E124"),sQuery(id+"F0.wireOp",EDGE,"E125"),sQuery(id+"F0.wireOp",EDGE,"E126"),sQuery(id+"F0.wireOp",EDGE,"E127"),sQuery(id+"F0.wireOp",EDGE,"E128"),sQuery(id+"F0.wireOp",EDGE,"E129"),sQuery(id+"F0.wireOp",EDGE,"E130"),sQuery(id+"F0.wireOp",EDGE,"E131"),sQuery(id+"F0.wireOp",EDGE,"E132"),sQuery(id+"F0.wireOp",EDGE,"E133"),sQuery(id+"F0.wireOp",EDGE,"E137"),sQuery(id+"F0.wireOp",EDGE,"E141"),sQuery(id+"F0.wireOp",EDGE,"E142"),sQuery(id+"F0.wireOp",EDGE,"E143"),sQuery(id+"F0.wireOp",EDGE,"E146"),sQuery(id+"F0.wireOp",EDGE,"E147"),sQuery(id+"F0.wireOp",EDGE,"E148"),sQuery(id+"F0.wireOp",EDGE,"E151"),sQuery(id+"F0.wireOp",EDGE,"E152"),sQuery(id+"F0.wireOp",EDGE,"E153"),sQuery(id+"F0.wireOp",EDGE,"E154"),sQuery(id+"F0.wireOp",EDGE,"E155"),sQuery(id+"F0.wireOp",EDGE,"E156"),sQuery(id+"F0.wireOp",EDGE,"E157"),sQuery(id+"F0.wireOp",EDGE,"E158"),sQuery(id+"F0.wireOp",EDGE,"E159"),sQuery(id+"F0.wireOp",EDGE,"E160"),sQuery(id+"F0.wireOp",EDGE,"E161"),sQuery(id+"F0.wireOp",EDGE,"E162"),sQuery(id+"F0.wireOp",EDGE,"E163"),sQuery(id+"F0.wireOp",EDGE,"E164"),sQuery(id+"F0.wireOp",EDGE,"E165"),sQuery(id+"F0.wireOp",EDGE,"E166"),sQuery(id+"F0.wireOp",EDGE,"E167"),sQuery(id+"F0.wireOp",EDGE,"E168"),sQuery(id+"F7.wireOp",EDGE,"E178"),sQuery(id+"F7.wireOp",EDGE,"E180"),sQuery(id+"F7.wireOp",EDGE,"E181"),sQuery(id+"F30.wireOp",EDGE,"E278.bottom"),sQuery(id+"F30.wireOp",EDGE,"E278.top"),sQuery(id+"F30.wireOp",EDGE,"E278.left"),sQuery(id+"F30.wireOp",EDGE,"E278.right")])],"isStart":false});
            var sketch = newSketch(context, id + "F35", { "sketchPlane" : qUnion([Q0])});
            skLineSegment(sketch, "E292", {"start": v(-762, -1403.47) * mm, "end": v(-762, -2419.47) * mm});
            skLineSegment(sketch, "E293", {"start": v(-762, -2419.47) * mm, "end": v(0, -2419.47) * mm});
            skLineSegment(sketch, "E294", {"start": v(0, -2419.47) * mm, "end": v(0, -1403.47) * mm});
            skLineSegment(sketch, "E295", {"start": v(0, -1403.47) * mm, "end": v(-762, -1403.47) * mm});
            skSolve(sketch);
        }
        {
            var Q0;
            Q0=qSketchRegion(id+"F35",true);
            extrude(context, id + "F36", {"entities" : qUnion([Q0]), "oppositeDirection" : true, "depth" : 76.2 * mm, "offsetDistance" : 25.4 * mm});
        }
        {
            var Q0;
            Q0=makeQuery(id+"F31.opExtrude","CAP_FACE",FACE,{"disambiguationData":[OSD([sQuery(id+"F0.wireOp",EDGE,"E1"),sQuery(id+"F0.wireOp",EDGE,"E2"),sQuery(id+"F0.wireOp",EDGE,"E3"),sQuery(id+"F0.wireOp",EDGE,"E4"),sQuery(id+"F0.wireOp",EDGE,"E6"),sQuery(id+"F0.wireOp",EDGE,"E7"),sQuery(id+"F0.wireOp",EDGE,"E8"),sQuery(id+"F0.wireOp",EDGE,"E9"),sQuery(id+"F0.wireOp",EDGE,"E10"),sQuery(id+"F0.wireOp",EDGE,"E11"),sQuery(id+"F0.wireOp",EDGE,"E12"),sQuery(id+"F0.wireOp",EDGE,"E13"),sQuery(id+"F0.wireOp",EDGE,"E19"),sQuery(id+"F0.wireOp",EDGE,"E20"),sQuery(id+"F0.wireOp",EDGE,"E21"),sQuery(id+"F0.wireOp",EDGE,"E22"),sQuery(id+"F0.wireOp",EDGE,"E24"),sQuery(id+"F0.wireOp",EDGE,"E25"),sQuery(id+"F0.wireOp",EDGE,"E26"),sQuery(id+"F0.wireOp",EDGE,"E27"),sQuery(id+"F0.wireOp",EDGE,"E28"),sQuery(id+"F0.wireOp",EDGE,"E29"),sQuery(id+"F0.wireOp",EDGE,"E30"),sQuery(id+"F0.wireOp",EDGE,"E31"),sQuery(id+"F0.wireOp",EDGE,"E32"),sQuery(id+"F0.wireOp",EDGE,"E34"),sQuery(id+"F0.wireOp",EDGE,"E35"),sQuery(id+"F0.wireOp",EDGE,"E36"),sQuery(id+"F0.wireOp",EDGE,"E37"),sQuery(id+"F0.wireOp",EDGE,"E38"),sQuery(id+"F0.wireOp",EDGE,"E39"),sQuery(id+"F0.wireOp",EDGE,"E40"),sQuery(id+"F0.wireOp",EDGE,"E41"),sQuery(id+"F0.wireOp",EDGE,"E42"),sQuery(id+"F0.wireOp",EDGE,"E43"),sQuery(id+"F0.wireOp",EDGE,"E44"),sQuery(id+"F0.wireOp",EDGE,"E45"),sQuery(id+"F0.wireOp",EDGE,"E46"),sQuery(id+"F0.wireOp",EDGE,"E47"),sQuery(id+"F0.wireOp",EDGE,"E48"),sQuery(id+"F0.wireOp",EDGE,"E49"),sQuery(id+"F0.wireOp",EDGE,"E50"),sQuery(id+"F0.wireOp",EDGE,"E51"),sQuery(id+"F0.wireOp",EDGE,"E52"),sQuery(id+"F0.wireOp",EDGE,"E53"),sQuery(id+"F0.wireOp",EDGE,"E54"),sQuery(id+"F0.wireOp",EDGE,"E55"),sQuery(id+"F0.wireOp",EDGE,"E56"),sQuery(id+"F0.wireOp",EDGE,"E57"),sQuery(id+"F0.wireOp",EDGE,"E58"),sQuery(id+"F0.wireOp",EDGE,"E59"),sQuery(id+"F0.wireOp",EDGE,"E60"),sQuery(id+"F0.wireOp",EDGE,"E61"),sQuery(id+"F0.wireOp",EDGE,"E62"),sQuery(id+"F0.wireOp",EDGE,"E63"),sQuery(id+"F0.wireOp",EDGE,"E64"),sQuery(id+"F0.wireOp",EDGE,"E65"),sQuery(id+"F0.wireOp",EDGE,"E66"),sQuery(id+"F0.wireOp",EDGE,"E67"),sQuery(id+"F0.wireOp",EDGE,"E68"),sQuery(id+"F0.wireOp",EDGE,"E69"),sQuery(id+"F0.wireOp",EDGE,"E70"),sQuery(id+"F0.wireOp",EDGE,"E71"),sQuery(id+"F0.wireOp",EDGE,"E72"),sQuery(id+"F0.wireOp",EDGE,"E73"),sQuery(id+"F0.wireOp",EDGE,"E74"),sQuery(id+"F0.wireOp",EDGE,"E75"),sQuery(id+"F0.wireOp",EDGE,"E76"),sQuery(id+"F0.wireOp",EDGE,"E77"),sQuery(id+"F0.wireOp",EDGE,"E78"),sQuery(id+"F0.wireOp",EDGE,"E79"),sQuery(id+"F0.wireOp",EDGE,"E80"),sQuery(id+"F0.wireOp",EDGE,"E81"),sQuery(id+"F0.wireOp",EDGE,"E82"),sQuery(id+"F0.wireOp",EDGE,"E83"),sQuery(id+"F0.wireOp",EDGE,"E84"),sQuery(id+"F0.wireOp",EDGE,"E85"),sQuery(id+"F0.wireOp",EDGE,"E86"),sQuery(id+"F0.wireOp",EDGE,"E87"),sQuery(id+"F0.wireOp",EDGE,"E88"),sQuery(id+"F0.wireOp",EDGE,"E89"),sQuery(id+"F0.wireOp",EDGE,"E90"),sQuery(id+"F0.wireOp",EDGE,"E91"),sQuery(id+"F0.wireOp",EDGE,"E94"),sQuery(id+"F0.wireOp",EDGE,"E95"),sQuery(id+"F0.wireOp",EDGE,"E98"),sQuery(id+"F0.wireOp",EDGE,"E99"),sQuery(id+"F0.wireOp",EDGE,"E100"),sQuery(id+"F0.wireOp",EDGE,"E101"),sQuery(id+"F0.wireOp",EDGE,"E102"),sQuery(id+"F0.wireOp",EDGE,"E103"),sQuery(id+"F0.wireOp",EDGE,"E104"),sQuery(id+"F0.wireOp",EDGE,"E105"),sQuery(id+"F0.wireOp",EDGE,"E106"),sQuery(id+"F0.wireOp",EDGE,"E107"),sQuery(id+"F0.wireOp",EDGE,"E108"),sQuery(id+"F0.wireOp",EDGE,"E109"),sQuery(id+"F0.wireOp",EDGE,"E110"),sQuery(id+"F0.wireOp",EDGE,"E111"),sQuery(id+"F0.wireOp",EDGE,"E112"),sQuery(id+"F0.wireOp",EDGE,"E113"),sQuery(id+"F0.wireOp",EDGE,"E114"),sQuery(id+"F0.wireOp",EDGE,"E115"),sQuery(id+"F0.wireOp",EDGE,"E116"),sQuery(id+"F0.wireOp",EDGE,"E117"),sQuery(id+"F0.wireOp",EDGE,"E118"),sQuery(id+"F0.wireOp",EDGE,"E119"),sQuery(id+"F0.wireOp",EDGE,"E120"),sQuery(id+"F0.wireOp",EDGE,"E121"),sQuery(id+"F0.wireOp",EDGE,"E122"),sQuery(id+"F0.wireOp",EDGE,"E123"),sQuery(id+"F0.wireOp",EDGE,"E124"),sQuery(id+"F0.wireOp",EDGE,"E125"),sQuery(id+"F0.wireOp",EDGE,"E126"),sQuery(id+"F0.wireOp",EDGE,"E127"),sQuery(id+"F0.wireOp",EDGE,"E128"),sQuery(id+"F0.wireOp",EDGE,"E129"),sQuery(id+"F0.wireOp",EDGE,"E130"),sQuery(id+"F0.wireOp",EDGE,"E131"),sQuery(id+"F0.wireOp",EDGE,"E132"),sQuery(id+"F0.wireOp",EDGE,"E133"),sQuery(id+"F0.wireOp",EDGE,"E137"),sQuery(id+"F0.wireOp",EDGE,"E141"),sQuery(id+"F0.wireOp",EDGE,"E142"),sQuery(id+"F0.wireOp",EDGE,"E143"),sQuery(id+"F0.wireOp",EDGE,"E146"),sQuery(id+"F0.wireOp",EDGE,"E147"),sQuery(id+"F0.wireOp",EDGE,"E148"),sQuery(id+"F0.wireOp",EDGE,"E151"),sQuery(id+"F0.wireOp",EDGE,"E152"),sQuery(id+"F0.wireOp",EDGE,"E153"),sQuery(id+"F0.wireOp",EDGE,"E154"),sQuery(id+"F0.wireOp",EDGE,"E155"),sQuery(id+"F0.wireOp",EDGE,"E156"),sQuery(id+"F0.wireOp",EDGE,"E157"),sQuery(id+"F0.wireOp",EDGE,"E158"),sQuery(id+"F0.wireOp",EDGE,"E159"),sQuery(id+"F0.wireOp",EDGE,"E160"),sQuery(id+"F0.wireOp",EDGE,"E161"),sQuery(id+"F0.wireOp",EDGE,"E162"),sQuery(id+"F0.wireOp",EDGE,"E163"),sQuery(id+"F0.wireOp",EDGE,"E164"),sQuery(id+"F0.wireOp",EDGE,"E165"),sQuery(id+"F0.wireOp",EDGE,"E166"),sQuery(id+"F0.wireOp",EDGE,"E167"),sQuery(id+"F0.wireOp",EDGE,"E168"),sQuery(id+"F7.wireOp",EDGE,"E178"),sQuery(id+"F7.wireOp",EDGE,"E180"),sQuery(id+"F7.wireOp",EDGE,"E181"),sQuery(id+"F30.wireOp",EDGE,"E278.bottom"),sQuery(id+"F30.wireOp",EDGE,"E278.top"),sQuery(id+"F30.wireOp",EDGE,"E278.left"),sQuery(id+"F30.wireOp",EDGE,"E278.right")])],"isStart":true});
            var sketch = newSketch(context, id + "F37", { "sketchPlane" : qUnion([Q0])});
            skLineSegment(sketch, "E296", {"start": v(231.53, 2589.71) * mm, "end": v(231.53, 1192.71) * mm});
            skLineSegment(sketch, "E297", {"start": v(231.53, 1192.71) * mm, "end": v(-635, 1192.71) * mm});
            skLineSegment(sketch, "E298", {"start": v(-635, 1192.71) * mm, "end": v(-762, 1192.71) * mm});
            skLineSegment(sketch, "E299", {"start": v(-762, 1192.71) * mm, "end": v(-993.52, 1192.71) * mm});
            skLineSegment(sketch, "E300", {"start": v(-993.52, 1192.71) * mm, "end": v(-993.52, 2419.47) * mm});
            skLineSegment(sketch, "E301", {"start": v(-993.52, 2419.47) * mm, "end": v(-993.52, 2630.21) * mm});
            skLineSegment(sketch, "E302", {"start": v(-993.52, 2630.21) * mm, "end": v(231.53, 2630.21) * mm});
            skLineSegment(sketch, "E303", {"start": v(231.53, 2630.21) * mm, "end": v(231.53, 2589.71) * mm});
            skLineSegment(sketch, "E304", {"start": v(-762, 2419.47) * mm, "end": v(-762, 1403.47) * mm});
            skLineSegment(sketch, "E305", {"start": v(-762, 1403.47) * mm, "end": v(0, 1403.47) * mm});
            skLineSegment(sketch, "E306", {"start": v(0, 1403.47) * mm, "end": v(0, 2419.47) * mm});
            skLineSegment(sketch, "E307", {"start": v(0, 2419.47) * mm, "end": v(-762, 2419.47) * mm});
            skSolve(sketch);
        }
        {
            var Q0;
            Q0=qSketchRegion(id+"F37",true);
            extrude(context, id + "F38", {"entities" : qUnion([Q0]), "oppositeDirection" : true, "depth" : 50.8 * mm, "offsetDistance" : 25.4 * mm});
        }
        {
            var Q0;
            Q0=makeQuery(id+"F38.opExtrude","CAP_FACE",FACE,{"disambiguationData":[OSD([sQuery(id+"F37.wireOp",EDGE,"E296"),sQuery(id+"F37.wireOp",EDGE,"E297"),sQuery(id+"F37.wireOp",EDGE,"E298"),sQuery(id+"F37.wireOp",EDGE,"E299"),sQuery(id+"F37.wireOp",EDGE,"E300"),sQuery(id+"F37.wireOp",EDGE,"E301"),sQuery(id+"F37.wireOp",EDGE,"E302"),sQuery(id+"F37.wireOp",EDGE,"E303"),sQuery(id+"F37.wireOp",EDGE,"E304"),sQuery(id+"F37.wireOp",EDGE,"E305"),sQuery(id+"F37.wireOp",EDGE,"E306"),sQuery(id+"F37.wireOp",EDGE,"E307")])],"isStart":true});
            extrude(context, id + "F39", {"entities" : qUnion([Q0]), "depth" : 25.4 * mm, "offsetDistance" : 25.4 * mm});
        }
        {
            var Q0;
            Q0=makeQuery(id+"F31.opExtrude","SWEPT_FACE",FACE,{"disambiguationData":[OSD([sQuery(id+"F30.wireOp",EDGE,"E278.left")])]});
            extrude(context, id + "F40", {"entities" : qUnion([Q0]), "operationType" : NewBodyOperationType.ADD, "depth" : 508 * mm, "offsetDistance" : 25.4 * mm});
        }
        {
            var Q0;
            {var subQ0=sQuery(id+"F30.wireOp",EDGE,"E278.bottom");Q0=makeQuery(id+"F40.boolean.opBoolean","MERGE",FACE,{"derivedFrom":[makeQuery(id+"F31.opExtrude","SWEPT_FACE",FACE,{"disambiguationData":[OSD([subQ0])]}),makeQuery(id+"F40.opExtrude","SWEPT_FACE",FACE,{"disambiguationData":[OSD([subQ0,sQuery(id+"F30.wireOp",EDGE,"E278.left")])]})]});}
            extrude(context, id + "F41", {"entities" : qUnion([Q0]), "operationType" : NewBodyOperationType.ADD, "depth" : 254 * mm, "offsetDistance" : 25.4 * mm});
        }
        {
            var Q0;
            {var subQ0=sQuery(id+"F30.wireOp",EDGE,"E278.top");Q0=makeQuery(id+"F40.boolean.opBoolean","MERGE",FACE,{"derivedFrom":[makeQuery(id+"F31.opExtrude","SWEPT_FACE",FACE,{"disambiguationData":[OSD([subQ0])]}),makeQuery(id+"F40.opExtrude","SWEPT_FACE",FACE,{"disambiguationData":[OSD([subQ0,sQuery(id+"F30.wireOp",EDGE,"E278.left")])]})]});}
            extrude(context, id + "F42", {"entities" : qUnion([Q0]), "operationType" : NewBodyOperationType.ADD, "depth" : 254 * mm, "offsetDistance" : 25.4 * mm});
        }
        {
            var Q0;
            Q0=makeQuery(id+"F39.opExtrude","SWEPT_FACE",FACE,{"disambiguationData":[OSD([sQuery(id+"F37.wireOp",EDGE,"E297"),sQuery(id+"F37.wireOp",EDGE,"E298"),sQuery(id+"F37.wireOp",EDGE,"E299")])]});
            var sketch = newSketch(context, id + "F43", { "sketchPlane" : qUnion([Q0])});
            skLineSegment(sketch, "E308", {"start": v(-993.52, 0) * mm, "end": v(-993.52, 25.4) * mm});
            skLineSegment(sketch, "E309.0", {"start": v(-635, 254) * mm, "end": v(-635, 0) * mm});
            skLineSegment(sketch, "E310", {"start": v(-993.52, 25.4) * mm, "end": v(-635, 25.4) * mm});
            skLineSegment(sketch, "E311", {"start": v(-635, 25.4) * mm, "end": v(-635, 0) * mm});
            skLineSegment(sketch, "E312", {"start": v(-993.52, 0) * mm, "end": v(-635, 0) * mm});
            skSolve(sketch);
        }
        {
            var Q0;
            Q0=makeQuery(id+"F10.opExtrude","CAP_FACE",FACE,{"disambiguationData":[OSD([sQuery(id+"F0.wireOp",EDGE,"E20"),sQuery(id+"F0.wireOp",EDGE,"E111"),sQuery(id+"F0.wireOp",EDGE,"E112"),sQuery(id+"F0.wireOp",EDGE,"E119"),sQuery(id+"F0.wireOp",EDGE,"E127"),sQuery(id+"F0.wireOp",EDGE,"E155")])],"isStart":false});
            var sketch = newSketch(context, id + "F44", { "sketchPlane" : qUnion([Q0])});
            skLineSegment(sketch, "E313.0", {"start": v(587.13, 254) * mm, "end": v(587.13, 0) * mm});
            skLineSegment(sketch, "E314", {"start": v(587.13, 0) * mm, "end": v(587.13, 25.4) * mm});
            skLineSegment(sketch, "E315", {"start": v(587.13, 25.4) * mm, "end": v(1346, 25.4) * mm});
            skLineSegment(sketch, "E316", {"start": v(1346, 0) * mm, "end": v(587.13, 0) * mm});
            skLineSegment(sketch, "E317.0", {"start": v(1349.13, 254) * mm, "end": v(1349.13, 0) * mm});
            skLineSegment(sketch, "E318", {"start": v(1346, 0) * mm, "end": v(1349.13, 0) * mm});
            skLineSegment(sketch, "E319", {"start": v(1349.13, 0) * mm, "end": v(1349.13, 25.4) * mm});
            skLineSegment(sketch, "E320", {"start": v(1349.13, 25.4) * mm, "end": v(1346, 25.4) * mm});
            skSolve(sketch);
        }
        {
            var Q0;
            {var subQ4=sQuery(id+"F44.wireOp",EDGE,"E315");var subQ6=sQuery(id+"F44.wireOp",EDGE,"E318");Q0=qUnion([makeQuery(id+"F44.imprint","IMPRINT",FACE,{"disambiguationData":[TD([[makeQuery(id+"F44.imprint","IMPRINT",EDGE,{"derivedFrom":subQ6}),1.0]])]}),makeQuery(id+"F44.imprint","IMPRINT",FACE,{"disambiguationData":[TD([[makeQuery(id+"F44.imprint","IMPRINT",EDGE,{"derivedFrom":subQ4}),1.0]])]})]);}
            extrude(context, id + "F45", {"entities" : qUnion([Q0]), "depth" : 381 * mm, "offsetDistance" : 25.4 * mm});
        }
        {
            var Q0;
            Q0=makeQuery(id+"F41.opExtrude","CAP_FACE",FACE,{"disambiguationData":[OSD([sQuery(id+"F30.wireOp",EDGE,"E278.bottom"),sQuery(id+"F30.wireOp",EDGE,"E278.left")])],"isStart":false});
            var sketch = newSketch(context, id + "F46", { "sketchPlane" : qUnion([Q0])});
            skLineSegment(sketch, "E321.0", {"start": v(-1612.75, 0) * mm, "end": v(2950.43, 0) * mm});
            skLineSegment(sketch, "E322.0", {"start": v(1349.13, 25.4) * mm, "end": v(587.13, 25.4) * mm});
            skLineSegment(sketch, "E323.0", {"start": v(1052.6, 0) * mm, "end": v(1052.6, 254) * mm});
            skLineSegment(sketch, "E324.0", {"start": v(1205, 254) * mm, "end": v(1205, 0) * mm});
            skLineSegment(sketch, "E325", {"start": v(1052.6, 0) * mm, "end": v(1052.6, -50.8) * mm});
            skLineSegment(sketch, "E326", {"start": v(1052.6, -50.8) * mm, "end": v(1205, -50.8) * mm});
            skLineSegment(sketch, "E327", {"start": v(1205, -50.8) * mm, "end": v(1205, 0) * mm});
            skLineSegment(sketch, "E328", {"start": v(1052.6, 0) * mm, "end": v(1205, 0) * mm});
            skSolve(sketch);
        }
        {
            var Q0;
            {var subQ2=sQuery(id+"F46.wireOp",EDGE,"E325");Q0=makeQuery(id+"F46.imprint","IMPRINT",FACE,{"disambiguationData":[TD([[makeQuery(id+"F46.imprint","IMPRINT",EDGE,{"derivedFrom":subQ2}),1.0]])]});}
            extrude(context, id + "F47", {"entities" : qUnion([Q0]), "operationType" : NewBodyOperationType.REMOVE, "oppositeDirection" : true, "depth" : 1016 * mm, "offsetDistance" : 25.4 * mm});
        }
        {
            var Q0;
            Q0=makeQuery(id+"F47.boolean.opBoolean","COPY",FACE,{"derivedFrom":makeQuery(id+"F47.opExtrude","CAP_FACE",FACE,{"disambiguationData":[OSD([sQuery(id+"F46.wireOp",EDGE,"E321.0"),sQuery(id+"F46.wireOp",EDGE,"E325"),sQuery(id+"F46.wireOp",EDGE,"E326"),sQuery(id+"F46.wireOp",EDGE,"E327")])],"isStart":false})});
            extrude(context, id + "F48", {"entities" : qUnion([Q0]), "depth" : 1016 * mm, "offsetDistance" : 25.4 * mm});
        }
        {
            var Q0;
            {var subQ0=sQuery(id+"F30.wireOp",EDGE,"E278.left");var subQ1=sQuery(id+"F30.wireOp",EDGE,"E278.top");var subQ2=sQuery(id+"F30.wireOp",EDGE,"E278.bottom");Q0=makeQuery(id+"F42.boolean.opBoolean","MERGE",FACE,{"derivedFrom":[makeQuery(id+"F41.boolean.opBoolean","MERGE",FACE,{"derivedFrom":[makeQuery(id+"F40.boolean.opBoolean","MERGE",FACE,{"derivedFrom":[makeQuery(id+"F31.opExtrude","CAP_FACE",FACE,{"disambiguationData":[OSD([sQuery(id+"F0.wireOp",EDGE,"E1"),sQuery(id+"F0.wireOp",EDGE,"E2"),sQuery(id+"F0.wireOp",EDGE,"E3"),sQuery(id+"F0.wireOp",EDGE,"E4"),sQuery(id+"F0.wireOp",EDGE,"E6"),sQuery(id+"F0.wireOp",EDGE,"E7"),sQuery(id+"F0.wireOp",EDGE,"E8"),sQuery(id+"F0.wireOp",EDGE,"E9"),sQuery(id+"F0.wireOp",EDGE,"E10"),sQuery(id+"F0.wireOp",EDGE,"E11"),sQuery(id+"F0.wireOp",EDGE,"E12"),sQuery(id+"F0.wireOp",EDGE,"E13"),sQuery(id+"F0.wireOp",EDGE,"E19"),sQuery(id+"F0.wireOp",EDGE,"E20"),sQuery(id+"F0.wireOp",EDGE,"E21"),sQuery(id+"F0.wireOp",EDGE,"E22"),sQuery(id+"F0.wireOp",EDGE,"E24"),sQuery(id+"F0.wireOp",EDGE,"E25"),sQuery(id+"F0.wireOp",EDGE,"E26"),sQuery(id+"F0.wireOp",EDGE,"E27"),sQuery(id+"F0.wireOp",EDGE,"E28"),sQuery(id+"F0.wireOp",EDGE,"E29"),sQuery(id+"F0.wireOp",EDGE,"E30"),sQuery(id+"F0.wireOp",EDGE,"E31"),sQuery(id+"F0.wireOp",EDGE,"E32"),sQuery(id+"F0.wireOp",EDGE,"E34"),sQuery(id+"F0.wireOp",EDGE,"E35"),sQuery(id+"F0.wireOp",EDGE,"E36"),sQuery(id+"F0.wireOp",EDGE,"E37"),sQuery(id+"F0.wireOp",EDGE,"E38"),sQuery(id+"F0.wireOp",EDGE,"E39"),sQuery(id+"F0.wireOp",EDGE,"E40"),sQuery(id+"F0.wireOp",EDGE,"E41"),sQuery(id+"F0.wireOp",EDGE,"E42"),sQuery(id+"F0.wireOp",EDGE,"E43"),sQuery(id+"F0.wireOp",EDGE,"E44"),sQuery(id+"F0.wireOp",EDGE,"E45"),sQuery(id+"F0.wireOp",EDGE,"E46"),sQuery(id+"F0.wireOp",EDGE,"E47"),sQuery(id+"F0.wireOp",EDGE,"E48"),sQuery(id+"F0.wireOp",EDGE,"E49"),sQuery(id+"F0.wireOp",EDGE,"E50"),sQuery(id+"F0.wireOp",EDGE,"E51"),sQuery(id+"F0.wireOp",EDGE,"E52"),sQuery(id+"F0.wireOp",EDGE,"E53"),sQuery(id+"F0.wireOp",EDGE,"E54"),sQuery(id+"F0.wireOp",EDGE,"E55"),sQuery(id+"F0.wireOp",EDGE,"E56"),sQuery(id+"F0.wireOp",EDGE,"E57"),sQuery(id+"F0.wireOp",EDGE,"E58"),sQuery(id+"F0.wireOp",EDGE,"E59"),sQuery(id+"F0.wireOp",EDGE,"E60"),sQuery(id+"F0.wireOp",EDGE,"E61"),sQuery(id+"F0.wireOp",EDGE,"E62"),sQuery(id+"F0.wireOp",EDGE,"E63"),sQuery(id+"F0.wireOp",EDGE,"E64"),sQuery(id+"F0.wireOp",EDGE,"E65"),sQuery(id+"F0.wireOp",EDGE,"E66"),sQuery(id+"F0.wireOp",EDGE,"E67"),sQuery(id+"F0.wireOp",EDGE,"E68"),sQuery(id+"F0.wireOp",EDGE,"E69"),sQuery(id+"F0.wireOp",EDGE,"E70"),sQuery(id+"F0.wireOp",EDGE,"E71"),sQuery(id+"F0.wireOp",EDGE,"E72"),sQuery(id+"F0.wireOp",EDGE,"E73"),sQuery(id+"F0.wireOp",EDGE,"E74"),sQuery(id+"F0.wireOp",EDGE,"E75"),sQuery(id+"F0.wireOp",EDGE,"E76"),sQuery(id+"F0.wireOp",EDGE,"E77"),sQuery(id+"F0.wireOp",EDGE,"E78"),sQuery(id+"F0.wireOp",EDGE,"E79"),sQuery(id+"F0.wireOp",EDGE,"E80"),sQuery(id+"F0.wireOp",EDGE,"E81"),sQuery(id+"F0.wireOp",EDGE,"E82"),sQuery(id+"F0.wireOp",EDGE,"E83"),sQuery(id+"F0.wireOp",EDGE,"E84"),sQuery(id+"F0.wireOp",EDGE,"E85"),sQuery(id+"F0.wireOp",EDGE,"E86"),sQuery(id+"F0.wireOp",EDGE,"E87"),sQuery(id+"F0.wireOp",EDGE,"E88"),sQuery(id+"F0.wireOp",EDGE,"E89"),sQuery(id+"F0.wireOp",EDGE,"E90"),sQuery(id+"F0.wireOp",EDGE,"E91"),sQuery(id+"F0.wireOp",EDGE,"E94"),sQuery(id+"F0.wireOp",EDGE,"E95"),sQuery(id+"F0.wireOp",EDGE,"E98"),sQuery(id+"F0.wireOp",EDGE,"E99"),sQuery(id+"F0.wireOp",EDGE,"E100"),sQuery(id+"F0.wireOp",EDGE,"E101"),sQuery(id+"F0.wireOp",EDGE,"E102"),sQuery(id+"F0.wireOp",EDGE,"E103"),sQuery(id+"F0.wireOp",EDGE,"E104"),sQuery(id+"F0.wireOp",EDGE,"E105"),sQuery(id+"F0.wireOp",EDGE,"E106"),sQuery(id+"F0.wireOp",EDGE,"E107"),sQuery(id+"F0.wireOp",EDGE,"E108"),sQuery(id+"F0.wireOp",EDGE,"E109"),sQuery(id+"F0.wireOp",EDGE,"E110"),sQuery(id+"F0.wireOp",EDGE,"E111"),sQuery(id+"F0.wireOp",EDGE,"E112"),sQuery(id+"F0.wireOp",EDGE,"E113"),sQuery(id+"F0.wireOp",EDGE,"E114"),sQuery(id+"F0.wireOp",EDGE,"E115"),sQuery(id+"F0.wireOp",EDGE,"E116"),sQuery(id+"F0.wireOp",EDGE,"E117"),sQuery(id+"F0.wireOp",EDGE,"E118"),sQuery(id+"F0.wireOp",EDGE,"E119"),sQuery(id+"F0.wireOp",EDGE,"E120"),sQuery(id+"F0.wireOp",EDGE,"E121"),sQuery(id+"F0.wireOp",EDGE,"E122"),sQuery(id+"F0.wireOp",EDGE,"E123"),sQuery(id+"F0.wireOp",EDGE,"E124"),sQuery(id+"F0.wireOp",EDGE,"E125"),sQuery(id+"F0.wireOp",EDGE,"E126"),sQuery(id+"F0.wireOp",EDGE,"E127"),sQuery(id+"F0.wireOp",EDGE,"E128"),sQuery(id+"F0.wireOp",EDGE,"E129"),sQuery(id+"F0.wireOp",EDGE,"E130"),sQuery(id+"F0.wireOp",EDGE,"E131"),sQuery(id+"F0.wireOp",EDGE,"E132"),sQuery(id+"F0.wireOp",EDGE,"E133"),sQuery(id+"F0.wireOp",EDGE,"E137"),sQuery(id+"F0.wireOp",EDGE,"E141"),sQuery(id+"F0.wireOp",EDGE,"E142"),sQuery(id+"F0.wireOp",EDGE,"E143"),sQuery(id+"F0.wireOp",EDGE,"E146"),sQuery(id+"F0.wireOp",EDGE,"E147"),sQuery(id+"F0.wireOp",EDGE,"E148"),sQuery(id+"F0.wireOp",EDGE,"E151"),sQuery(id+"F0.wireOp",EDGE,"E152"),sQuery(id+"F0.wireOp",EDGE,"E153"),sQuery(id+"F0.wireOp",EDGE,"E154"),sQuery(id+"F0.wireOp",EDGE,"E155"),sQuery(id+"F0.wireOp",EDGE,"E156"),sQuery(id+"F0.wireOp",EDGE,"E157"),sQuery(id+"F0.wireOp",EDGE,"E158"),sQuery(id+"F0.wireOp",EDGE,"E159"),sQuery(id+"F0.wireOp",EDGE,"E160"),sQuery(id+"F0.wireOp",EDGE,"E161"),sQuery(id+"F0.wireOp",EDGE,"E162"),sQuery(id+"F0.wireOp",EDGE,"E163"),sQuery(id+"F0.wireOp",EDGE,"E164"),sQuery(id+"F0.wireOp",EDGE,"E165"),sQuery(id+"F0.wireOp",EDGE,"E166"),sQuery(id+"F0.wireOp",EDGE,"E167"),sQuery(id+"F0.wireOp",EDGE,"E168"),sQuery(id+"F7.wireOp",EDGE,"E178"),sQuery(id+"F7.wireOp",EDGE,"E180"),sQuery(id+"F7.wireOp",EDGE,"E181"),subQ2,subQ1,subQ0,sQuery(id+"F30.wireOp",EDGE,"E278.right")])],"isStart":true}),makeQuery(id+"F40.opExtrude","SWEPT_FACE",FACE,{"disambiguationData":[OSD([subQ0]),TDD([makeQuery(id+"F31.opExtrude","CAP_EDGE",EDGE,{"disambiguationData":[OSD([subQ0])],"isStart":true})])]})]}),makeQuery(id+"F41.opExtrude","SWEPT_FACE",FACE,{"disambiguationData":[OSD([subQ2,subQ0]),TDD([makeQuery(id+"F40.boolean.opBoolean","MERGE",EDGE,{"derivedFrom":[makeQuery(id+"F31.opExtrude","CAP_EDGE",EDGE,{"disambiguationData":[OSD([subQ2])],"isStart":true}),makeQuery(id+"F40.opExtrude","SWEPT_EDGE",EDGE,{"disambiguationData":[OSD([subQ2,subQ0]),TDD([makeQuery(id+"F31.opExtrude","CAP_VERTEX",VERTEX,{"disambiguationData":[OSD([subQ2,subQ0])],"isStart":true})])]})]})])]})]}),makeQuery(id+"F42.opExtrude","SWEPT_FACE",FACE,{"disambiguationData":[OSD([subQ1,subQ0]),TDD([makeQuery(id+"F40.boolean.opBoolean","MERGE",EDGE,{"derivedFrom":[makeQuery(id+"F31.opExtrude","CAP_EDGE",EDGE,{"disambiguationData":[OSD([subQ1])],"isStart":true}),makeQuery(id+"F40.opExtrude","SWEPT_EDGE",EDGE,{"disambiguationData":[OSD([subQ1,subQ0]),TDD([makeQuery(id+"F31.opExtrude","CAP_VERTEX",VERTEX,{"disambiguationData":[OSD([subQ1,subQ0])],"isStart":true})])]})]})])]})]});}
            var sketch = newSketch(context, id + "F49", { "sketchPlane" : qUnion([Q0])});
            skLineSegment(sketch, "E329", {"start": v(1052.6, -851.15) * mm, "end": v(900.2, -851.15) * mm});
            skLineSegment(sketch, "E330", {"start": v(900.2, -851.15) * mm, "end": v(900.2, -698.75) * mm});
            skLineSegment(sketch, "E331", {"start": v(900.2, -698.75) * mm, "end": v(1052.6, -698.75) * mm});
            skLineSegment(sketch, "E332", {"start": v(1052.6, -698.75) * mm, "end": v(1052.6, -851.15) * mm});
            skLineSegment(sketch, "E333", {"start": v(1052.6, -851.15) * mm, "end": v(1205, -851.15) * mm});
            skLineSegment(sketch, "E334.MirrorCS", {"start": v(1205, -698.75) * mm, "end": v(1205, -851.15) * mm});
            skLineSegment(sketch, "E335.MirrorCS", {"start": v(1357.4, -698.75) * mm, "end": v(1205, -698.75) * mm});
            skLineSegment(sketch, "E336.MirrorCS", {"start": v(1357.4, -851.15) * mm, "end": v(1357.4, -698.75) * mm});
            skLineSegment(sketch, "E337.MirrorCS", {"start": v(1205, -851.15) * mm, "end": v(1357.4, -851.15) * mm});
            skSolve(sketch);
        }
        {
            var Q0;
            Q0=qSketchRegion(id+"F49",true);
            extrude(context, id + "F50", {"entities" : qUnion([Q0]), "depth" : 177.8 * mm, "offsetDistance" : 25.4 * mm});
        }
        {
            var Q0;
            Q0=makeQuery(id+"F50.opExtrude","SWEPT_FACE",FACE,{"disambiguationData":[OSD([sQuery(id+"F49.wireOp",EDGE,"E336.MirrorCS")])]});
            var sketch = newSketch(context, id + "F51", { "sketchPlane" : qUnion([Q0])});
            skLineSegment(sketch, "E338", {"start": v(-851.15, 0) * mm, "end": v(-698.75, 0) * mm});
            skLineSegment(sketch, "E339", {"start": v(-774.95, 0) * mm, "end": v(-800.35, 0) * mm});
            skLineSegment(sketch, "E340", {"start": v(-800.35, 0) * mm, "end": v(-749.55, 0) * mm});
            skLineSegment(sketch, "E341", {"start": v(-749.55, 0) * mm, "end": v(-749.55, 101.6) * mm});
            skLineSegment(sketch, "E342", {"start": v(-749.55, 101.6) * mm, "end": v(-800.35, 101.6) * mm});
            skLineSegment(sketch, "E343", {"start": v(-800.35, 101.6) * mm, "end": v(-800.35, 0) * mm});
            skSolve(sketch);
        }
        {
            var Q0;
            {var subQ0=sQuery(id+"F51.wireOp",EDGE,"E341");Q0=makeQuery(id+"F51.imprint","IMPRINT",FACE,{"disambiguationData":[TD([[makeQuery(id+"F51.imprint","IMPRINT",EDGE,{"derivedFrom":subQ0}),1.0]])]});}
            extrude(context, id + "F52", {"entities" : qUnion([Q0]), "depth" : 1524 * mm, "offsetDistance" : 25.4 * mm});
        }
        {
            var Q0;
            {var subQ0=sQuery(id+"F30.wireOp",EDGE,"E278.left");var subQ1=sQuery(id+"F30.wireOp",EDGE,"E278.top");var subQ2=sQuery(id+"F30.wireOp",EDGE,"E278.bottom");Q0=makeQuery(id+"F42.boolean.opBoolean","MERGE",FACE,{"derivedFrom":[makeQuery(id+"F41.boolean.opBoolean","MERGE",FACE,{"derivedFrom":[makeQuery(id+"F40.boolean.opBoolean","MERGE",FACE,{"derivedFrom":[makeQuery(id+"F31.opExtrude","CAP_FACE",FACE,{"disambiguationData":[OSD([sQuery(id+"F0.wireOp",EDGE,"E1"),sQuery(id+"F0.wireOp",EDGE,"E2"),sQuery(id+"F0.wireOp",EDGE,"E3"),sQuery(id+"F0.wireOp",EDGE,"E4"),sQuery(id+"F0.wireOp",EDGE,"E6"),sQuery(id+"F0.wireOp",EDGE,"E7"),sQuery(id+"F0.wireOp",EDGE,"E8"),sQuery(id+"F0.wireOp",EDGE,"E9"),sQuery(id+"F0.wireOp",EDGE,"E10"),sQuery(id+"F0.wireOp",EDGE,"E11"),sQuery(id+"F0.wireOp",EDGE,"E12"),sQuery(id+"F0.wireOp",EDGE,"E13"),sQuery(id+"F0.wireOp",EDGE,"E19"),sQuery(id+"F0.wireOp",EDGE,"E20"),sQuery(id+"F0.wireOp",EDGE,"E21"),sQuery(id+"F0.wireOp",EDGE,"E22"),sQuery(id+"F0.wireOp",EDGE,"E24"),sQuery(id+"F0.wireOp",EDGE,"E25"),sQuery(id+"F0.wireOp",EDGE,"E26"),sQuery(id+"F0.wireOp",EDGE,"E27"),sQuery(id+"F0.wireOp",EDGE,"E28"),sQuery(id+"F0.wireOp",EDGE,"E29"),sQuery(id+"F0.wireOp",EDGE,"E30"),sQuery(id+"F0.wireOp",EDGE,"E31"),sQuery(id+"F0.wireOp",EDGE,"E32"),sQuery(id+"F0.wireOp",EDGE,"E34"),sQuery(id+"F0.wireOp",EDGE,"E35"),sQuery(id+"F0.wireOp",EDGE,"E36"),sQuery(id+"F0.wireOp",EDGE,"E37"),sQuery(id+"F0.wireOp",EDGE,"E38"),sQuery(id+"F0.wireOp",EDGE,"E39"),sQuery(id+"F0.wireOp",EDGE,"E40"),sQuery(id+"F0.wireOp",EDGE,"E41"),sQuery(id+"F0.wireOp",EDGE,"E42"),sQuery(id+"F0.wireOp",EDGE,"E43"),sQuery(id+"F0.wireOp",EDGE,"E44"),sQuery(id+"F0.wireOp",EDGE,"E45"),sQuery(id+"F0.wireOp",EDGE,"E46"),sQuery(id+"F0.wireOp",EDGE,"E47"),sQuery(id+"F0.wireOp",EDGE,"E48"),sQuery(id+"F0.wireOp",EDGE,"E49"),sQuery(id+"F0.wireOp",EDGE,"E50"),sQuery(id+"F0.wireOp",EDGE,"E51"),sQuery(id+"F0.wireOp",EDGE,"E52"),sQuery(id+"F0.wireOp",EDGE,"E53"),sQuery(id+"F0.wireOp",EDGE,"E54"),sQuery(id+"F0.wireOp",EDGE,"E55"),sQuery(id+"F0.wireOp",EDGE,"E56"),sQuery(id+"F0.wireOp",EDGE,"E57"),sQuery(id+"F0.wireOp",EDGE,"E58"),sQuery(id+"F0.wireOp",EDGE,"E59"),sQuery(id+"F0.wireOp",EDGE,"E60"),sQuery(id+"F0.wireOp",EDGE,"E61"),sQuery(id+"F0.wireOp",EDGE,"E62"),sQuery(id+"F0.wireOp",EDGE,"E63"),sQuery(id+"F0.wireOp",EDGE,"E64"),sQuery(id+"F0.wireOp",EDGE,"E65"),sQuery(id+"F0.wireOp",EDGE,"E66"),sQuery(id+"F0.wireOp",EDGE,"E67"),sQuery(id+"F0.wireOp",EDGE,"E68"),sQuery(id+"F0.wireOp",EDGE,"E69"),sQuery(id+"F0.wireOp",EDGE,"E70"),sQuery(id+"F0.wireOp",EDGE,"E71"),sQuery(id+"F0.wireOp",EDGE,"E72"),sQuery(id+"F0.wireOp",EDGE,"E73"),sQuery(id+"F0.wireOp",EDGE,"E74"),sQuery(id+"F0.wireOp",EDGE,"E75"),sQuery(id+"F0.wireOp",EDGE,"E76"),sQuery(id+"F0.wireOp",EDGE,"E77"),sQuery(id+"F0.wireOp",EDGE,"E78"),sQuery(id+"F0.wireOp",EDGE,"E79"),sQuery(id+"F0.wireOp",EDGE,"E80"),sQuery(id+"F0.wireOp",EDGE,"E81"),sQuery(id+"F0.wireOp",EDGE,"E82"),sQuery(id+"F0.wireOp",EDGE,"E83"),sQuery(id+"F0.wireOp",EDGE,"E84"),sQuery(id+"F0.wireOp",EDGE,"E85"),sQuery(id+"F0.wireOp",EDGE,"E86"),sQuery(id+"F0.wireOp",EDGE,"E87"),sQuery(id+"F0.wireOp",EDGE,"E88"),sQuery(id+"F0.wireOp",EDGE,"E89"),sQuery(id+"F0.wireOp",EDGE,"E90"),sQuery(id+"F0.wireOp",EDGE,"E91"),sQuery(id+"F0.wireOp",EDGE,"E94"),sQuery(id+"F0.wireOp",EDGE,"E95"),sQuery(id+"F0.wireOp",EDGE,"E98"),sQuery(id+"F0.wireOp",EDGE,"E99"),sQuery(id+"F0.wireOp",EDGE,"E100"),sQuery(id+"F0.wireOp",EDGE,"E101"),sQuery(id+"F0.wireOp",EDGE,"E102"),sQuery(id+"F0.wireOp",EDGE,"E103"),sQuery(id+"F0.wireOp",EDGE,"E104"),sQuery(id+"F0.wireOp",EDGE,"E105"),sQuery(id+"F0.wireOp",EDGE,"E106"),sQuery(id+"F0.wireOp",EDGE,"E107"),sQuery(id+"F0.wireOp",EDGE,"E108"),sQuery(id+"F0.wireOp",EDGE,"E109"),sQuery(id+"F0.wireOp",EDGE,"E110"),sQuery(id+"F0.wireOp",EDGE,"E111"),sQuery(id+"F0.wireOp",EDGE,"E112"),sQuery(id+"F0.wireOp",EDGE,"E113"),sQuery(id+"F0.wireOp",EDGE,"E114"),sQuery(id+"F0.wireOp",EDGE,"E115"),sQuery(id+"F0.wireOp",EDGE,"E116"),sQuery(id+"F0.wireOp",EDGE,"E117"),sQuery(id+"F0.wireOp",EDGE,"E118"),sQuery(id+"F0.wireOp",EDGE,"E119"),sQuery(id+"F0.wireOp",EDGE,"E120"),sQuery(id+"F0.wireOp",EDGE,"E121"),sQuery(id+"F0.wireOp",EDGE,"E122"),sQuery(id+"F0.wireOp",EDGE,"E123"),sQuery(id+"F0.wireOp",EDGE,"E124"),sQuery(id+"F0.wireOp",EDGE,"E125"),sQuery(id+"F0.wireOp",EDGE,"E126"),sQuery(id+"F0.wireOp",EDGE,"E127"),sQuery(id+"F0.wireOp",EDGE,"E128"),sQuery(id+"F0.wireOp",EDGE,"E129"),sQuery(id+"F0.wireOp",EDGE,"E130"),sQuery(id+"F0.wireOp",EDGE,"E131"),sQuery(id+"F0.wireOp",EDGE,"E132"),sQuery(id+"F0.wireOp",EDGE,"E133"),sQuery(id+"F0.wireOp",EDGE,"E137"),sQuery(id+"F0.wireOp",EDGE,"E141"),sQuery(id+"F0.wireOp",EDGE,"E142"),sQuery(id+"F0.wireOp",EDGE,"E143"),sQuery(id+"F0.wireOp",EDGE,"E146"),sQuery(id+"F0.wireOp",EDGE,"E147"),sQuery(id+"F0.wireOp",EDGE,"E148"),sQuery(id+"F0.wireOp",EDGE,"E151"),sQuery(id+"F0.wireOp",EDGE,"E152"),sQuery(id+"F0.wireOp",EDGE,"E153"),sQuery(id+"F0.wireOp",EDGE,"E154"),sQuery(id+"F0.wireOp",EDGE,"E155"),sQuery(id+"F0.wireOp",EDGE,"E156"),sQuery(id+"F0.wireOp",EDGE,"E157"),sQuery(id+"F0.wireOp",EDGE,"E158"),sQuery(id+"F0.wireOp",EDGE,"E159"),sQuery(id+"F0.wireOp",EDGE,"E160"),sQuery(id+"F0.wireOp",EDGE,"E161"),sQuery(id+"F0.wireOp",EDGE,"E162"),sQuery(id+"F0.wireOp",EDGE,"E163"),sQuery(id+"F0.wireOp",EDGE,"E164"),sQuery(id+"F0.wireOp",EDGE,"E165"),sQuery(id+"F0.wireOp",EDGE,"E166"),sQuery(id+"F0.wireOp",EDGE,"E167"),sQuery(id+"F0.wireOp",EDGE,"E168"),sQuery(id+"F7.wireOp",EDGE,"E178"),sQuery(id+"F7.wireOp",EDGE,"E180"),sQuery(id+"F7.wireOp",EDGE,"E181"),subQ2,subQ1,subQ0,sQuery(id+"F30.wireOp",EDGE,"E278.right")])],"isStart":true}),makeQuery(id+"F40.opExtrude","SWEPT_FACE",FACE,{"disambiguationData":[OSD([subQ0]),TDD([makeQuery(id+"F31.opExtrude","CAP_EDGE",EDGE,{"disambiguationData":[OSD([subQ0])],"isStart":true})])]})]}),makeQuery(id+"F41.opExtrude","SWEPT_FACE",FACE,{"disambiguationData":[OSD([subQ2,subQ0]),TDD([makeQuery(id+"F40.boolean.opBoolean","MERGE",EDGE,{"derivedFrom":[makeQuery(id+"F31.opExtrude","CAP_EDGE",EDGE,{"disambiguationData":[OSD([subQ2])],"isStart":true}),makeQuery(id+"F40.opExtrude","SWEPT_EDGE",EDGE,{"disambiguationData":[OSD([subQ2,subQ0]),TDD([makeQuery(id+"F31.opExtrude","CAP_VERTEX",VERTEX,{"disambiguationData":[OSD([subQ2,subQ0])],"isStart":true})])]})]})])]})]}),makeQuery(id+"F42.opExtrude","SWEPT_FACE",FACE,{"disambiguationData":[OSD([subQ1,subQ0]),TDD([makeQuery(id+"F40.boolean.opBoolean","MERGE",EDGE,{"derivedFrom":[makeQuery(id+"F31.opExtrude","CAP_EDGE",EDGE,{"disambiguationData":[OSD([subQ1])],"isStart":true}),makeQuery(id+"F40.opExtrude","SWEPT_EDGE",EDGE,{"disambiguationData":[OSD([subQ1,subQ0]),TDD([makeQuery(id+"F31.opExtrude","CAP_VERTEX",VERTEX,{"disambiguationData":[OSD([subQ1,subQ0])],"isStart":true})])]})]})])]})]});}
            var sketch = newSketch(context, id + "F53", { "sketchPlane" : qUnion([Q0])});
            skLineSegment(sketch, "E344", {"start": v(2950.43, -851.15) * mm, "end": v(2798.03, -851.15) * mm});
            skLineSegment(sketch, "E345", {"start": v(2798.03, -851.15) * mm, "end": v(2798.03, -698.75) * mm});
            skLineSegment(sketch, "E346", {"start": v(2798.03, -698.75) * mm, "end": v(2950.43, -698.75) * mm});
            skLineSegment(sketch, "E347", {"start": v(2950.43, -698.75) * mm, "end": v(2950.43, -851.15) * mm});
            skSolve(sketch);
        }
        {
            var Q0;
            Q0=qSketchRegion(id+"F53",true);
            extrude(context, id + "F54", {"entities" : qUnion([Q0]), "depth" : 177.8 * mm, "offsetDistance" : 25.4 * mm});
        }
        {
            var Q0;
            {var subQ0=sQuery(id+"F30.wireOp",EDGE,"E278.left");var subQ1=sQuery(id+"F30.wireOp",EDGE,"E278.top");var subQ2=sQuery(id+"F30.wireOp",EDGE,"E278.bottom");Q0=makeQuery(id+"F42.boolean.opBoolean","MERGE",FACE,{"derivedFrom":[makeQuery(id+"F41.boolean.opBoolean","MERGE",FACE,{"derivedFrom":[makeQuery(id+"F40.boolean.opBoolean","MERGE",FACE,{"derivedFrom":[makeQuery(id+"F31.opExtrude","CAP_FACE",FACE,{"disambiguationData":[OSD([sQuery(id+"F0.wireOp",EDGE,"E1"),sQuery(id+"F0.wireOp",EDGE,"E2"),sQuery(id+"F0.wireOp",EDGE,"E3"),sQuery(id+"F0.wireOp",EDGE,"E4"),sQuery(id+"F0.wireOp",EDGE,"E6"),sQuery(id+"F0.wireOp",EDGE,"E7"),sQuery(id+"F0.wireOp",EDGE,"E8"),sQuery(id+"F0.wireOp",EDGE,"E9"),sQuery(id+"F0.wireOp",EDGE,"E10"),sQuery(id+"F0.wireOp",EDGE,"E11"),sQuery(id+"F0.wireOp",EDGE,"E12"),sQuery(id+"F0.wireOp",EDGE,"E13"),sQuery(id+"F0.wireOp",EDGE,"E19"),sQuery(id+"F0.wireOp",EDGE,"E20"),sQuery(id+"F0.wireOp",EDGE,"E21"),sQuery(id+"F0.wireOp",EDGE,"E22"),sQuery(id+"F0.wireOp",EDGE,"E24"),sQuery(id+"F0.wireOp",EDGE,"E25"),sQuery(id+"F0.wireOp",EDGE,"E26"),sQuery(id+"F0.wireOp",EDGE,"E27"),sQuery(id+"F0.wireOp",EDGE,"E28"),sQuery(id+"F0.wireOp",EDGE,"E29"),sQuery(id+"F0.wireOp",EDGE,"E30"),sQuery(id+"F0.wireOp",EDGE,"E31"),sQuery(id+"F0.wireOp",EDGE,"E32"),sQuery(id+"F0.wireOp",EDGE,"E34"),sQuery(id+"F0.wireOp",EDGE,"E35"),sQuery(id+"F0.wireOp",EDGE,"E36"),sQuery(id+"F0.wireOp",EDGE,"E37"),sQuery(id+"F0.wireOp",EDGE,"E38"),sQuery(id+"F0.wireOp",EDGE,"E39"),sQuery(id+"F0.wireOp",EDGE,"E40"),sQuery(id+"F0.wireOp",EDGE,"E41"),sQuery(id+"F0.wireOp",EDGE,"E42"),sQuery(id+"F0.wireOp",EDGE,"E43"),sQuery(id+"F0.wireOp",EDGE,"E44"),sQuery(id+"F0.wireOp",EDGE,"E45"),sQuery(id+"F0.wireOp",EDGE,"E46"),sQuery(id+"F0.wireOp",EDGE,"E47"),sQuery(id+"F0.wireOp",EDGE,"E48"),sQuery(id+"F0.wireOp",EDGE,"E49"),sQuery(id+"F0.wireOp",EDGE,"E50"),sQuery(id+"F0.wireOp",EDGE,"E51"),sQuery(id+"F0.wireOp",EDGE,"E52"),sQuery(id+"F0.wireOp",EDGE,"E53"),sQuery(id+"F0.wireOp",EDGE,"E54"),sQuery(id+"F0.wireOp",EDGE,"E55"),sQuery(id+"F0.wireOp",EDGE,"E56"),sQuery(id+"F0.wireOp",EDGE,"E57"),sQuery(id+"F0.wireOp",EDGE,"E58"),sQuery(id+"F0.wireOp",EDGE,"E59"),sQuery(id+"F0.wireOp",EDGE,"E60"),sQuery(id+"F0.wireOp",EDGE,"E61"),sQuery(id+"F0.wireOp",EDGE,"E62"),sQuery(id+"F0.wireOp",EDGE,"E63"),sQuery(id+"F0.wireOp",EDGE,"E64"),sQuery(id+"F0.wireOp",EDGE,"E65"),sQuery(id+"F0.wireOp",EDGE,"E66"),sQuery(id+"F0.wireOp",EDGE,"E67"),sQuery(id+"F0.wireOp",EDGE,"E68"),sQuery(id+"F0.wireOp",EDGE,"E69"),sQuery(id+"F0.wireOp",EDGE,"E70"),sQuery(id+"F0.wireOp",EDGE,"E71"),sQuery(id+"F0.wireOp",EDGE,"E72"),sQuery(id+"F0.wireOp",EDGE,"E73"),sQuery(id+"F0.wireOp",EDGE,"E74"),sQuery(id+"F0.wireOp",EDGE,"E75"),sQuery(id+"F0.wireOp",EDGE,"E76"),sQuery(id+"F0.wireOp",EDGE,"E77"),sQuery(id+"F0.wireOp",EDGE,"E78"),sQuery(id+"F0.wireOp",EDGE,"E79"),sQuery(id+"F0.wireOp",EDGE,"E80"),sQuery(id+"F0.wireOp",EDGE,"E81"),sQuery(id+"F0.wireOp",EDGE,"E82"),sQuery(id+"F0.wireOp",EDGE,"E83"),sQuery(id+"F0.wireOp",EDGE,"E84"),sQuery(id+"F0.wireOp",EDGE,"E85"),sQuery(id+"F0.wireOp",EDGE,"E86"),sQuery(id+"F0.wireOp",EDGE,"E87"),sQuery(id+"F0.wireOp",EDGE,"E88"),sQuery(id+"F0.wireOp",EDGE,"E89"),sQuery(id+"F0.wireOp",EDGE,"E90"),sQuery(id+"F0.wireOp",EDGE,"E91"),sQuery(id+"F0.wireOp",EDGE,"E94"),sQuery(id+"F0.wireOp",EDGE,"E95"),sQuery(id+"F0.wireOp",EDGE,"E98"),sQuery(id+"F0.wireOp",EDGE,"E99"),sQuery(id+"F0.wireOp",EDGE,"E100"),sQuery(id+"F0.wireOp",EDGE,"E101"),sQuery(id+"F0.wireOp",EDGE,"E102"),sQuery(id+"F0.wireOp",EDGE,"E103"),sQuery(id+"F0.wireOp",EDGE,"E104"),sQuery(id+"F0.wireOp",EDGE,"E105"),sQuery(id+"F0.wireOp",EDGE,"E106"),sQuery(id+"F0.wireOp",EDGE,"E107"),sQuery(id+"F0.wireOp",EDGE,"E108"),sQuery(id+"F0.wireOp",EDGE,"E109"),sQuery(id+"F0.wireOp",EDGE,"E110"),sQuery(id+"F0.wireOp",EDGE,"E111"),sQuery(id+"F0.wireOp",EDGE,"E112"),sQuery(id+"F0.wireOp",EDGE,"E113"),sQuery(id+"F0.wireOp",EDGE,"E114"),sQuery(id+"F0.wireOp",EDGE,"E115"),sQuery(id+"F0.wireOp",EDGE,"E116"),sQuery(id+"F0.wireOp",EDGE,"E117"),sQuery(id+"F0.wireOp",EDGE,"E118"),sQuery(id+"F0.wireOp",EDGE,"E119"),sQuery(id+"F0.wireOp",EDGE,"E120"),sQuery(id+"F0.wireOp",EDGE,"E121"),sQuery(id+"F0.wireOp",EDGE,"E122"),sQuery(id+"F0.wireOp",EDGE,"E123"),sQuery(id+"F0.wireOp",EDGE,"E124"),sQuery(id+"F0.wireOp",EDGE,"E125"),sQuery(id+"F0.wireOp",EDGE,"E126"),sQuery(id+"F0.wireOp",EDGE,"E127"),sQuery(id+"F0.wireOp",EDGE,"E128"),sQuery(id+"F0.wireOp",EDGE,"E129"),sQuery(id+"F0.wireOp",EDGE,"E130"),sQuery(id+"F0.wireOp",EDGE,"E131"),sQuery(id+"F0.wireOp",EDGE,"E132"),sQuery(id+"F0.wireOp",EDGE,"E133"),sQuery(id+"F0.wireOp",EDGE,"E137"),sQuery(id+"F0.wireOp",EDGE,"E141"),sQuery(id+"F0.wireOp",EDGE,"E142"),sQuery(id+"F0.wireOp",EDGE,"E143"),sQuery(id+"F0.wireOp",EDGE,"E146"),sQuery(id+"F0.wireOp",EDGE,"E147"),sQuery(id+"F0.wireOp",EDGE,"E148"),sQuery(id+"F0.wireOp",EDGE,"E151"),sQuery(id+"F0.wireOp",EDGE,"E152"),sQuery(id+"F0.wireOp",EDGE,"E153"),sQuery(id+"F0.wireOp",EDGE,"E154"),sQuery(id+"F0.wireOp",EDGE,"E155"),sQuery(id+"F0.wireOp",EDGE,"E156"),sQuery(id+"F0.wireOp",EDGE,"E157"),sQuery(id+"F0.wireOp",EDGE,"E158"),sQuery(id+"F0.wireOp",EDGE,"E159"),sQuery(id+"F0.wireOp",EDGE,"E160"),sQuery(id+"F0.wireOp",EDGE,"E161"),sQuery(id+"F0.wireOp",EDGE,"E162"),sQuery(id+"F0.wireOp",EDGE,"E163"),sQuery(id+"F0.wireOp",EDGE,"E164"),sQuery(id+"F0.wireOp",EDGE,"E165"),sQuery(id+"F0.wireOp",EDGE,"E166"),sQuery(id+"F0.wireOp",EDGE,"E167"),sQuery(id+"F0.wireOp",EDGE,"E168"),sQuery(id+"F7.wireOp",EDGE,"E178"),sQuery(id+"F7.wireOp",EDGE,"E180"),sQuery(id+"F7.wireOp",EDGE,"E181"),subQ2,subQ1,subQ0,sQuery(id+"F30.wireOp",EDGE,"E278.right")])],"isStart":true}),makeQuery(id+"F40.opExtrude","SWEPT_FACE",FACE,{"disambiguationData":[OSD([subQ0]),TDD([makeQuery(id+"F31.opExtrude","CAP_EDGE",EDGE,{"disambiguationData":[OSD([subQ0])],"isStart":true})])]})]}),makeQuery(id+"F41.opExtrude","SWEPT_FACE",FACE,{"disambiguationData":[OSD([subQ2,subQ0]),TDD([makeQuery(id+"F40.boolean.opBoolean","MERGE",EDGE,{"derivedFrom":[makeQuery(id+"F31.opExtrude","CAP_EDGE",EDGE,{"disambiguationData":[OSD([subQ2])],"isStart":true}),makeQuery(id+"F40.opExtrude","SWEPT_EDGE",EDGE,{"disambiguationData":[OSD([subQ2,subQ0]),TDD([makeQuery(id+"F31.opExtrude","CAP_VERTEX",VERTEX,{"disambiguationData":[OSD([subQ2,subQ0])],"isStart":true})])]})]})])]})]}),makeQuery(id+"F42.opExtrude","SWEPT_FACE",FACE,{"disambiguationData":[OSD([subQ1,subQ0]),TDD([makeQuery(id+"F40.boolean.opBoolean","MERGE",EDGE,{"derivedFrom":[makeQuery(id+"F31.opExtrude","CAP_EDGE",EDGE,{"disambiguationData":[OSD([subQ1])],"isStart":true}),makeQuery(id+"F40.opExtrude","SWEPT_EDGE",EDGE,{"disambiguationData":[OSD([subQ1,subQ0]),TDD([makeQuery(id+"F31.opExtrude","CAP_VERTEX",VERTEX,{"disambiguationData":[OSD([subQ1,subQ0])],"isStart":true})])]})]})])]})]});}
            var sketch = newSketch(context, id + "F55", { "sketchPlane" : qUnion([Q0])});
            skLineSegment(sketch, "E348", {"start": v(2950.43, 3391.36) * mm, "end": v(2798.03, 3391.36) * mm});
            skLineSegment(sketch, "E349", {"start": v(2798.03, 3391.36) * mm, "end": v(2798.03, 3238.96) * mm});
            skLineSegment(sketch, "E350", {"start": v(2798.03, 3238.96) * mm, "end": v(2950.43, 3238.96) * mm});
            skLineSegment(sketch, "E351", {"start": v(2950.43, 3238.96) * mm, "end": v(2950.43, 3391.36) * mm});
            skLineSegment(sketch, "E352", {"start": v(-1612.75, 3391.36) * mm, "end": v(-1612.75, 3238.96) * mm});
            skLineSegment(sketch, "E353", {"start": v(-1612.75, 3238.96) * mm, "end": v(-1460.35, 3238.96) * mm});
            skLineSegment(sketch, "E354", {"start": v(-1460.35, 3238.96) * mm, "end": v(-1460.35, 3391.36) * mm});
            skLineSegment(sketch, "E355", {"start": v(-1460.35, 3391.36) * mm, "end": v(-1612.75, 3391.36) * mm});
            skLineSegment(sketch, "E356", {"start": v(-1612.75, -851.15) * mm, "end": v(-1612.75, -698.75) * mm});
            skLineSegment(sketch, "E357", {"start": v(-1612.75, -698.75) * mm, "end": v(-1460.35, -698.75) * mm});
            skLineSegment(sketch, "E358", {"start": v(-1460.35, -698.75) * mm, "end": v(-1460.35, -851.15) * mm});
            skLineSegment(sketch, "E359", {"start": v(-1460.35, -851.15) * mm, "end": v(-1612.75, -851.15) * mm});
            skSolve(sketch);
        }
        {
            var Q0;
            Q0=qSketchRegion(id+"F55",true);
            extrude(context, id + "F56", {"entities" : qUnion([Q0]), "depth" : 177.8 * mm, "offsetDistance" : 25.4 * mm});
        }
        {
            var Q0;
            Q0=makeQuery(id+"F56.opExtrude","SWEPT_FACE",FACE,{"disambiguationData":[OSD([sQuery(id+"F55.wireOp",EDGE,"E350")])]});
            var sketch = newSketch(context, id + "F57", { "sketchPlane" : qUnion([Q0])});
            skLineSegment(sketch, "E360", {"start": v(2798.03, 0) * mm, "end": v(2950.43, 0) * mm});
            skLineSegment(sketch, "E361", {"start": v(2950.43, 0) * mm, "end": v(2874.23, 0) * mm});
            skLineSegment(sketch, "E362", {"start": v(2874.23, 0) * mm, "end": v(2848.83, 0) * mm});
            skLineSegment(sketch, "E363", {"start": v(2848.83, 0) * mm, "end": v(2899.63, 0) * mm});
            skLineSegment(sketch, "E364", {"start": v(2899.63, 0) * mm, "end": v(2899.63, 101.6) * mm});
            skLineSegment(sketch, "E365", {"start": v(2899.63, 101.6) * mm, "end": v(2848.83, 101.6) * mm});
            skLineSegment(sketch, "E366", {"start": v(2848.83, 101.6) * mm, "end": v(2848.83, 0) * mm});
            skSolve(sketch);
        }
        {
            var Q0;
            {var subQ0=sQuery(id+"F57.wireOp",EDGE,"E364");Q0=makeQuery(id+"F57.imprint","IMPRINT",FACE,{"disambiguationData":[TD([[makeQuery(id+"F57.imprint","IMPRINT",EDGE,{"derivedFrom":subQ0}),1.0]])]});}
            extrude(context, id + "F58", {"entities" : qUnion([Q0]), "depth" : 3937 * mm, "offsetDistance" : 25.4 * mm});
        }
        {
            var Q0;
            Q0=makeQuery(id+"F56.opExtrude","SWEPT_FACE",FACE,{"disambiguationData":[OSD([sQuery(id+"F55.wireOp",EDGE,"E354")])]});
            var sketch = newSketch(context, id + "F59", { "sketchPlane" : qUnion([Q0])});
            skLineSegment(sketch, "E367", {"start": v(3315.16, 0) * mm, "end": v(3289.76, 0) * mm});
            skLineSegment(sketch, "E368", {"start": v(3289.76, 0) * mm, "end": v(3340.56, 0) * mm});
            skLineSegment(sketch, "E369", {"start": v(3340.56, 0) * mm, "end": v(3340.56, 101.6) * mm});
            skLineSegment(sketch, "E370", {"start": v(3340.56, 101.6) * mm, "end": v(3289.76, 101.6) * mm});
            skLineSegment(sketch, "E371", {"start": v(3289.76, 101.6) * mm, "end": v(3289.76, 0) * mm});
            skSolve(sketch);
        }
        {
            var Q0;
            Q0=qSketchRegion(id+"F59",true);
            extrude(context, id + "F60", {"entities" : qUnion([Q0]), "depth" : 4318 * mm, "offsetDistance" : 25.4 * mm});
        }
        {
            var Q0;
            Q0=makeQuery(id+"F56.opExtrude","SWEPT_FACE",FACE,{"disambiguationData":[OSD([sQuery(id+"F55.wireOp",EDGE,"E353")])]});
            var sketch = newSketch(context, id + "F61", { "sketchPlane" : qUnion([Q0])});
            skLineSegment(sketch, "E372", {"start": v(-1536.55, 0) * mm, "end": v(-1561.95, 0) * mm});
            skLineSegment(sketch, "E373", {"start": v(-1561.95, 0) * mm, "end": v(-1511.15, 0) * mm});
            skLineSegment(sketch, "E374", {"start": v(-1511.15, 0) * mm, "end": v(-1511.15, 101.6) * mm});
            skLineSegment(sketch, "E375", {"start": v(-1511.15, 101.6) * mm, "end": v(-1561.95, 101.6) * mm});
            skLineSegment(sketch, "E376", {"start": v(-1561.95, 101.6) * mm, "end": v(-1561.95, 0) * mm});
            skSolve(sketch);
        }
        {
            var Q0;
            Q0=qSketchRegion(id+"F61",true);
            extrude(context, id + "F62", {"entities" : qUnion([Q0]), "depth" : 4064 * mm, "offsetDistance" : 25.4 * mm});
        }
        {
            var Q0;
            Q0=makeQuery(id+"F56.opExtrude","SWEPT_FACE",FACE,{"disambiguationData":[OSD([sQuery(id+"F55.wireOp",EDGE,"E358")])]});
            var sketch = newSketch(context, id + "F63", { "sketchPlane" : qUnion([Q0])});
            skLineSegment(sketch, "E377", {"start": v(-774.95, 0) * mm, "end": v(-800.35, 0) * mm});
            skLineSegment(sketch, "E378", {"start": v(-800.35, 0) * mm, "end": v(-749.55, 0) * mm});
            skLineSegment(sketch, "E379", {"start": v(-749.55, 0) * mm, "end": v(-749.55, 101.6) * mm});
            skLineSegment(sketch, "E380", {"start": v(-749.55, 101.6) * mm, "end": v(-800.35, 101.6) * mm});
            skLineSegment(sketch, "E381", {"start": v(-800.35, 101.6) * mm, "end": v(-800.35, 0) * mm});
            skSolve(sketch);
        }
        {
            var Q0;
            Q0=makeQuery(id+"F1.opExtrude","SWEPT_FACE",FACE,{"disambiguationData":[OSD([sQuery(id+"F0.wireOp",EDGE,"E7"),sQuery(id+"F0.wireOp",EDGE,"E94")])]});
            var sketch = newSketch(context, id + "F64", { "sketchPlane" : qUnion([Q0])});
            skLineSegment(sketch, "E382", {"start": v(-23.93, 254) * mm, "end": v(-23.93, 0) * mm});
            skLineSegment(sketch, "E383", {"start": v(-23.93, 0) * mm, "end": v(-277.93, 0) * mm});
            skLineSegment(sketch, "E384", {"start": v(-277.93, 0) * mm, "end": v(230.07, 0) * mm});
            skLineSegment(sketch, "E385.0.0", {"start": v(1052.6, -50.8) * mm, "end": v(1052.6, 0) * mm});
            skLineSegment(sketch, "E385.0.2", {"start": v(-1612.75, 0) * mm, "end": v(-1612.75, -50.8) * mm});
            skLineSegment(sketch, "E386", {"start": v(-277.93, 0) * mm, "end": v(-277.93, -50.8) * mm});
            skLineSegment(sketch, "E387", {"start": v(-277.93, -50.8) * mm, "end": v(230.07, -50.8) * mm});
            skLineSegment(sketch, "E388", {"start": v(230.07, -50.8) * mm, "end": v(230.07, 0) * mm});
            skSolve(sketch);
        }
        {
            var Q0;
            Q0=makeQuery(id+"F64.imprint","IMPRINT",FACE,{"disambiguationData":[TD([[makeQuery(id+"F64.imprint","IMPRINT",EDGE,{"derivedFrom":sQuery(id+"F64.wireOp",EDGE,"E383")}),1.0]])]});
            extrude(context, id + "F65", {"entities" : qUnion([Q0]), "operationType" : NewBodyOperationType.ADD, "depth" : 1905 * mm, "offsetDistance" : 25.4 * mm});
        }
        {
            var Q0;
            Q0=makeQuery(id+"F65.opExtrude","CAP_FACE",FACE,{"disambiguationData":[OSD([sQuery(id+"F64.wireOp",EDGE,"E383"),sQuery(id+"F64.wireOp",EDGE,"E384"),sQuery(id+"F64.wireOp",EDGE,"E386"),sQuery(id+"F64.wireOp",EDGE,"E387"),sQuery(id+"F64.wireOp",EDGE,"E388")])],"isStart":false});
            extrude(context, id + "F66", {"entities" : qUnion([Q0]), "operationType" : NewBodyOperationType.REMOVE, "oppositeDirection" : true, "depth" : 1905 * mm, "offsetDistance" : 25.4 * mm});
        }
        {
            var Q0;
            Q0=makeQuery(id+"F64.imprint","IMPRINT",FACE,{"disambiguationData":[TD([[makeQuery(id+"F64.imprint","IMPRINT",EDGE,{"derivedFrom":sQuery(id+"F64.wireOp",EDGE,"E383")}),1.0]])]});
            extrude(context, id + "F67", {"entities" : qUnion([Q0]), "depth" : 799.47 * mm, "offsetDistance" : 25.4 * mm});
        }
        {
            var Q0;
            Q0=makeQuery(id+"F1.opExtrude","SWEPT_FACE",FACE,{"disambiguationData":[OSD([sQuery(id+"F0.wireOp",EDGE,"E7"),sQuery(id+"F0.wireOp",EDGE,"E94")])]});
            var sketch = newSketch(context, id + "F68", { "sketchPlane" : qUnion([Q0])});
            skLineSegment(sketch, "E389.0", {"start": v(230.07, 0) * mm, "end": v(-277.93, 0) * mm});
            skLineSegment(sketch, "E390", {"start": v(-277.93, 0) * mm, "end": v(-277.93, 152.4) * mm});
            skLineSegment(sketch, "E391", {"start": v(-277.93, 152.4) * mm, "end": v(230.07, 152.4) * mm});
            skLineSegment(sketch, "E392", {"start": v(230.07, 152.4) * mm, "end": v(230.07, 0) * mm});
            skSolve(sketch);
        }
        {
            var Q0;
            Q0=qSketchRegion(id+"F68",true);
            extrude(context, id + "F69", {"entities" : qUnion([Q0]), "operationType" : NewBodyOperationType.REMOVE, "oppositeDirection" : true, "depth" : 76.2 * mm, "offsetDistance" : 25.4 * mm});
        }
        {
            var Q0;
            {var subQ0=sQuery(id+"F30.wireOp",EDGE,"E278.left");var subQ1=sQuery(id+"F30.wireOp",EDGE,"E278.top");var subQ2=sQuery(id+"F30.wireOp",EDGE,"E278.bottom");Q0=makeQuery(id+"F65.boolean.opBoolean","MERGE",FACE,{"derivedFrom":[makeQuery(id+"F42.boolean.opBoolean","MERGE",FACE,{"derivedFrom":[makeQuery(id+"F41.boolean.opBoolean","MERGE",FACE,{"derivedFrom":[makeQuery(id+"F40.boolean.opBoolean","MERGE",FACE,{"derivedFrom":[makeQuery(id+"F31.opExtrude","CAP_FACE",FACE,{"disambiguationData":[OSD([sQuery(id+"F0.wireOp",EDGE,"E1"),sQuery(id+"F0.wireOp",EDGE,"E2"),sQuery(id+"F0.wireOp",EDGE,"E3"),sQuery(id+"F0.wireOp",EDGE,"E4"),sQuery(id+"F0.wireOp",EDGE,"E6"),sQuery(id+"F0.wireOp",EDGE,"E7"),sQuery(id+"F0.wireOp",EDGE,"E8"),sQuery(id+"F0.wireOp",EDGE,"E9"),sQuery(id+"F0.wireOp",EDGE,"E10"),sQuery(id+"F0.wireOp",EDGE,"E11"),sQuery(id+"F0.wireOp",EDGE,"E12"),sQuery(id+"F0.wireOp",EDGE,"E13"),sQuery(id+"F0.wireOp",EDGE,"E19"),sQuery(id+"F0.wireOp",EDGE,"E20"),sQuery(id+"F0.wireOp",EDGE,"E21"),sQuery(id+"F0.wireOp",EDGE,"E22"),sQuery(id+"F0.wireOp",EDGE,"E24"),sQuery(id+"F0.wireOp",EDGE,"E25"),sQuery(id+"F0.wireOp",EDGE,"E26"),sQuery(id+"F0.wireOp",EDGE,"E27"),sQuery(id+"F0.wireOp",EDGE,"E28"),sQuery(id+"F0.wireOp",EDGE,"E29"),sQuery(id+"F0.wireOp",EDGE,"E30"),sQuery(id+"F0.wireOp",EDGE,"E31"),sQuery(id+"F0.wireOp",EDGE,"E32"),sQuery(id+"F0.wireOp",EDGE,"E34"),sQuery(id+"F0.wireOp",EDGE,"E35"),sQuery(id+"F0.wireOp",EDGE,"E36"),sQuery(id+"F0.wireOp",EDGE,"E37"),sQuery(id+"F0.wireOp",EDGE,"E38"),sQuery(id+"F0.wireOp",EDGE,"E39"),sQuery(id+"F0.wireOp",EDGE,"E40"),sQuery(id+"F0.wireOp",EDGE,"E41"),sQuery(id+"F0.wireOp",EDGE,"E42"),sQuery(id+"F0.wireOp",EDGE,"E43"),sQuery(id+"F0.wireOp",EDGE,"E44"),sQuery(id+"F0.wireOp",EDGE,"E45"),sQuery(id+"F0.wireOp",EDGE,"E46"),sQuery(id+"F0.wireOp",EDGE,"E47"),sQuery(id+"F0.wireOp",EDGE,"E48"),sQuery(id+"F0.wireOp",EDGE,"E49"),sQuery(id+"F0.wireOp",EDGE,"E50"),sQuery(id+"F0.wireOp",EDGE,"E51"),sQuery(id+"F0.wireOp",EDGE,"E52"),sQuery(id+"F0.wireOp",EDGE,"E53"),sQuery(id+"F0.wireOp",EDGE,"E54"),sQuery(id+"F0.wireOp",EDGE,"E55"),sQuery(id+"F0.wireOp",EDGE,"E56"),sQuery(id+"F0.wireOp",EDGE,"E57"),sQuery(id+"F0.wireOp",EDGE,"E58"),sQuery(id+"F0.wireOp",EDGE,"E59"),sQuery(id+"F0.wireOp",EDGE,"E60"),sQuery(id+"F0.wireOp",EDGE,"E61"),sQuery(id+"F0.wireOp",EDGE,"E62"),sQuery(id+"F0.wireOp",EDGE,"E63"),sQuery(id+"F0.wireOp",EDGE,"E64"),sQuery(id+"F0.wireOp",EDGE,"E65"),sQuery(id+"F0.wireOp",EDGE,"E66"),sQuery(id+"F0.wireOp",EDGE,"E67"),sQuery(id+"F0.wireOp",EDGE,"E68"),sQuery(id+"F0.wireOp",EDGE,"E69"),sQuery(id+"F0.wireOp",EDGE,"E70"),sQuery(id+"F0.wireOp",EDGE,"E71"),sQuery(id+"F0.wireOp",EDGE,"E72"),sQuery(id+"F0.wireOp",EDGE,"E73"),sQuery(id+"F0.wireOp",EDGE,"E74"),sQuery(id+"F0.wireOp",EDGE,"E75"),sQuery(id+"F0.wireOp",EDGE,"E76"),sQuery(id+"F0.wireOp",EDGE,"E77"),sQuery(id+"F0.wireOp",EDGE,"E78"),sQuery(id+"F0.wireOp",EDGE,"E79"),sQuery(id+"F0.wireOp",EDGE,"E80"),sQuery(id+"F0.wireOp",EDGE,"E81"),sQuery(id+"F0.wireOp",EDGE,"E82"),sQuery(id+"F0.wireOp",EDGE,"E83"),sQuery(id+"F0.wireOp",EDGE,"E84"),sQuery(id+"F0.wireOp",EDGE,"E85"),sQuery(id+"F0.wireOp",EDGE,"E86"),sQuery(id+"F0.wireOp",EDGE,"E87"),sQuery(id+"F0.wireOp",EDGE,"E88"),sQuery(id+"F0.wireOp",EDGE,"E89"),sQuery(id+"F0.wireOp",EDGE,"E90"),sQuery(id+"F0.wireOp",EDGE,"E91"),sQuery(id+"F0.wireOp",EDGE,"E94"),sQuery(id+"F0.wireOp",EDGE,"E95"),sQuery(id+"F0.wireOp",EDGE,"E98"),sQuery(id+"F0.wireOp",EDGE,"E99"),sQuery(id+"F0.wireOp",EDGE,"E100"),sQuery(id+"F0.wireOp",EDGE,"E101"),sQuery(id+"F0.wireOp",EDGE,"E102"),sQuery(id+"F0.wireOp",EDGE,"E103"),sQuery(id+"F0.wireOp",EDGE,"E104"),sQuery(id+"F0.wireOp",EDGE,"E105"),sQuery(id+"F0.wireOp",EDGE,"E106"),sQuery(id+"F0.wireOp",EDGE,"E107"),sQuery(id+"F0.wireOp",EDGE,"E108"),sQuery(id+"F0.wireOp",EDGE,"E109"),sQuery(id+"F0.wireOp",EDGE,"E110"),sQuery(id+"F0.wireOp",EDGE,"E111"),sQuery(id+"F0.wireOp",EDGE,"E112"),sQuery(id+"F0.wireOp",EDGE,"E113"),sQuery(id+"F0.wireOp",EDGE,"E114"),sQuery(id+"F0.wireOp",EDGE,"E115"),sQuery(id+"F0.wireOp",EDGE,"E116"),sQuery(id+"F0.wireOp",EDGE,"E117"),sQuery(id+"F0.wireOp",EDGE,"E118"),sQuery(id+"F0.wireOp",EDGE,"E119"),sQuery(id+"F0.wireOp",EDGE,"E120"),sQuery(id+"F0.wireOp",EDGE,"E121"),sQuery(id+"F0.wireOp",EDGE,"E122"),sQuery(id+"F0.wireOp",EDGE,"E123"),sQuery(id+"F0.wireOp",EDGE,"E124"),sQuery(id+"F0.wireOp",EDGE,"E125"),sQuery(id+"F0.wireOp",EDGE,"E126"),sQuery(id+"F0.wireOp",EDGE,"E128"),sQuery(id+"F0.wireOp",EDGE,"E129"),sQuery(id+"F0.wireOp",EDGE,"E130"),sQuery(id+"F0.wireOp",EDGE,"E131"),sQuery(id+"F0.wireOp",EDGE,"E132"),sQuery(id+"F0.wireOp",EDGE,"E133"),sQuery(id+"F0.wireOp",EDGE,"E137"),sQuery(id+"F0.wireOp",EDGE,"E141"),sQuery(id+"F0.wireOp",EDGE,"E142"),sQuery(id+"F0.wireOp",EDGE,"E143"),sQuery(id+"F0.wireOp",EDGE,"E146"),sQuery(id+"F0.wireOp",EDGE,"E147"),sQuery(id+"F0.wireOp",EDGE,"E148"),sQuery(id+"F0.wireOp",EDGE,"E151"),sQuery(id+"F0.wireOp",EDGE,"E152"),sQuery(id+"F0.wireOp",EDGE,"E153"),sQuery(id+"F0.wireOp",EDGE,"E154"),sQuery(id+"F0.wireOp",EDGE,"E155"),sQuery(id+"F0.wireOp",EDGE,"E156"),sQuery(id+"F0.wireOp",EDGE,"E157"),sQuery(id+"F0.wireOp",EDGE,"E158"),sQuery(id+"F0.wireOp",EDGE,"E159"),sQuery(id+"F0.wireOp",EDGE,"E160"),sQuery(id+"F0.wireOp",EDGE,"E161"),sQuery(id+"F0.wireOp",EDGE,"E162"),sQuery(id+"F0.wireOp",EDGE,"E163"),sQuery(id+"F0.wireOp",EDGE,"E164"),sQuery(id+"F0.wireOp",EDGE,"E165"),sQuery(id+"F0.wireOp",EDGE,"E166"),sQuery(id+"F0.wireOp",EDGE,"E167"),sQuery(id+"F0.wireOp",EDGE,"E168"),sQuery(id+"F7.wireOp",EDGE,"E178"),sQuery(id+"F7.wireOp",EDGE,"E180"),sQuery(id+"F7.wireOp",EDGE,"E181"),subQ2,subQ1,subQ0,sQuery(id+"F30.wireOp",EDGE,"E278.right")])],"isStart":true}),makeQuery(id+"F40.opExtrude","SWEPT_FACE",FACE,{"disambiguationData":[OSD([subQ0]),TDD([makeQuery(id+"F31.opExtrude","CAP_EDGE",EDGE,{"disambiguationData":[OSD([subQ0])],"isStart":true})])]})]}),makeQuery(id+"F41.opExtrude","SWEPT_FACE",FACE,{"disambiguationData":[OSD([subQ2,subQ0]),TDD([makeQuery(id+"F40.boolean.opBoolean","MERGE",EDGE,{"derivedFrom":[makeQuery(id+"F31.opExtrude","CAP_EDGE",EDGE,{"disambiguationData":[OSD([subQ2])],"isStart":true}),makeQuery(id+"F40.opExtrude","SWEPT_EDGE",EDGE,{"disambiguationData":[OSD([subQ2,subQ0]),TDD([makeQuery(id+"F31.opExtrude","CAP_VERTEX",VERTEX,{"disambiguationData":[OSD([subQ2,subQ0])],"isStart":true})])]})]})])]})]}),makeQuery(id+"F42.opExtrude","SWEPT_FACE",FACE,{"disambiguationData":[OSD([subQ1,subQ0]),TDD([makeQuery(id+"F40.boolean.opBoolean","MERGE",EDGE,{"derivedFrom":[makeQuery(id+"F31.opExtrude","CAP_EDGE",EDGE,{"disambiguationData":[OSD([subQ1])],"isStart":true}),makeQuery(id+"F40.opExtrude","SWEPT_EDGE",EDGE,{"disambiguationData":[OSD([subQ1,subQ0]),TDD([makeQuery(id+"F31.opExtrude","CAP_VERTEX",VERTEX,{"disambiguationData":[OSD([subQ1,subQ0])],"isStart":true})])]})]})])]})]}),makeQuery(id+"F65.opExtrude","SWEPT_FACE",FACE,{"disambiguationData":[OSD([sQuery(id+"F64.wireOp",EDGE,"E383"),sQuery(id+"F64.wireOp",EDGE,"E384")])]})]});}
            var sketch = newSketch(context, id + "F70", { "sketchPlane" : qUnion([Q0])});
            skLineSegment(sketch, "E393", {"start": v(-277.93, -851.15) * mm, "end": v(-277.93, -698.75) * mm});
            skLineSegment(sketch, "E394", {"start": v(-277.93, -698.75) * mm, "end": v(-430.33, -698.75) * mm});
            skLineSegment(sketch, "E395", {"start": v(-430.33, -698.75) * mm, "end": v(-430.33, -851.15) * mm});
            skLineSegment(sketch, "E396", {"start": v(-430.33, -851.15) * mm, "end": v(-277.93, -851.15) * mm});
            skLineSegment(sketch, "E397", {"start": v(230.07, -851.15) * mm, "end": v(230.07, -698.75) * mm});
            skLineSegment(sketch, "E398", {"start": v(230.07, -698.75) * mm, "end": v(382.47, -698.75) * mm});
            skLineSegment(sketch, "E399", {"start": v(382.47, -698.75) * mm, "end": v(382.47, -851.15) * mm});
            skLineSegment(sketch, "E400", {"start": v(382.47, -851.15) * mm, "end": v(230.07, -851.15) * mm});
            skSolve(sketch);
        }
        {
            var Q0;
            Q0=qSketchRegion(id+"F70",true);
            extrude(context, id + "F71", {"entities" : qUnion([Q0]), "depth" : 177.8 * mm, "offsetDistance" : 25.4 * mm});
        }
        {
            var Q0;
            {var subQ0=sQuery(id+"F63.wireOp",EDGE,"E379");Q0=makeQuery(id+"F63.imprint","IMPRINT",FACE,{"disambiguationData":[TD([[makeQuery(id+"F63.imprint","IMPRINT",EDGE,{"derivedFrom":subQ0}),1.0]])]});}
            extrude(context, id + "F72", {"entities" : qUnion([Q0]), "depth" : 1143 * mm, "offsetDistance" : 25.4 * mm});
        }
        {
            var Q0;
            Q0=makeQuery(id+"F71.opExtrude","SWEPT_FACE",FACE,{"disambiguationData":[OSD([sQuery(id+"F70.wireOp",EDGE,"E399")])]});
            var sketch = newSketch(context, id + "F73", { "sketchPlane" : qUnion([Q0])});
            skLineSegment(sketch, "E401", {"start": v(-774.95, 0) * mm, "end": v(-800.35, 0) * mm});
            skLineSegment(sketch, "E402", {"start": v(-800.35, 0) * mm, "end": v(-749.55, 0) * mm});
            skLineSegment(sketch, "E403", {"start": v(-749.55, 0) * mm, "end": v(-749.55, 101.6) * mm});
            skLineSegment(sketch, "E404", {"start": v(-749.55, 101.6) * mm, "end": v(-800.35, 101.6) * mm});
            skLineSegment(sketch, "E405", {"start": v(-800.35, 101.6) * mm, "end": v(-800.35, 0) * mm});
            skSolve(sketch);
        }
        {
            var Q0;
            Q0=qSketchRegion(id+"F73",true);
            extrude(context, id + "F74", {"entities" : qUnion([Q0]), "depth" : 635 * mm, "offsetDistance" : 25.4 * mm});
        }
    });
